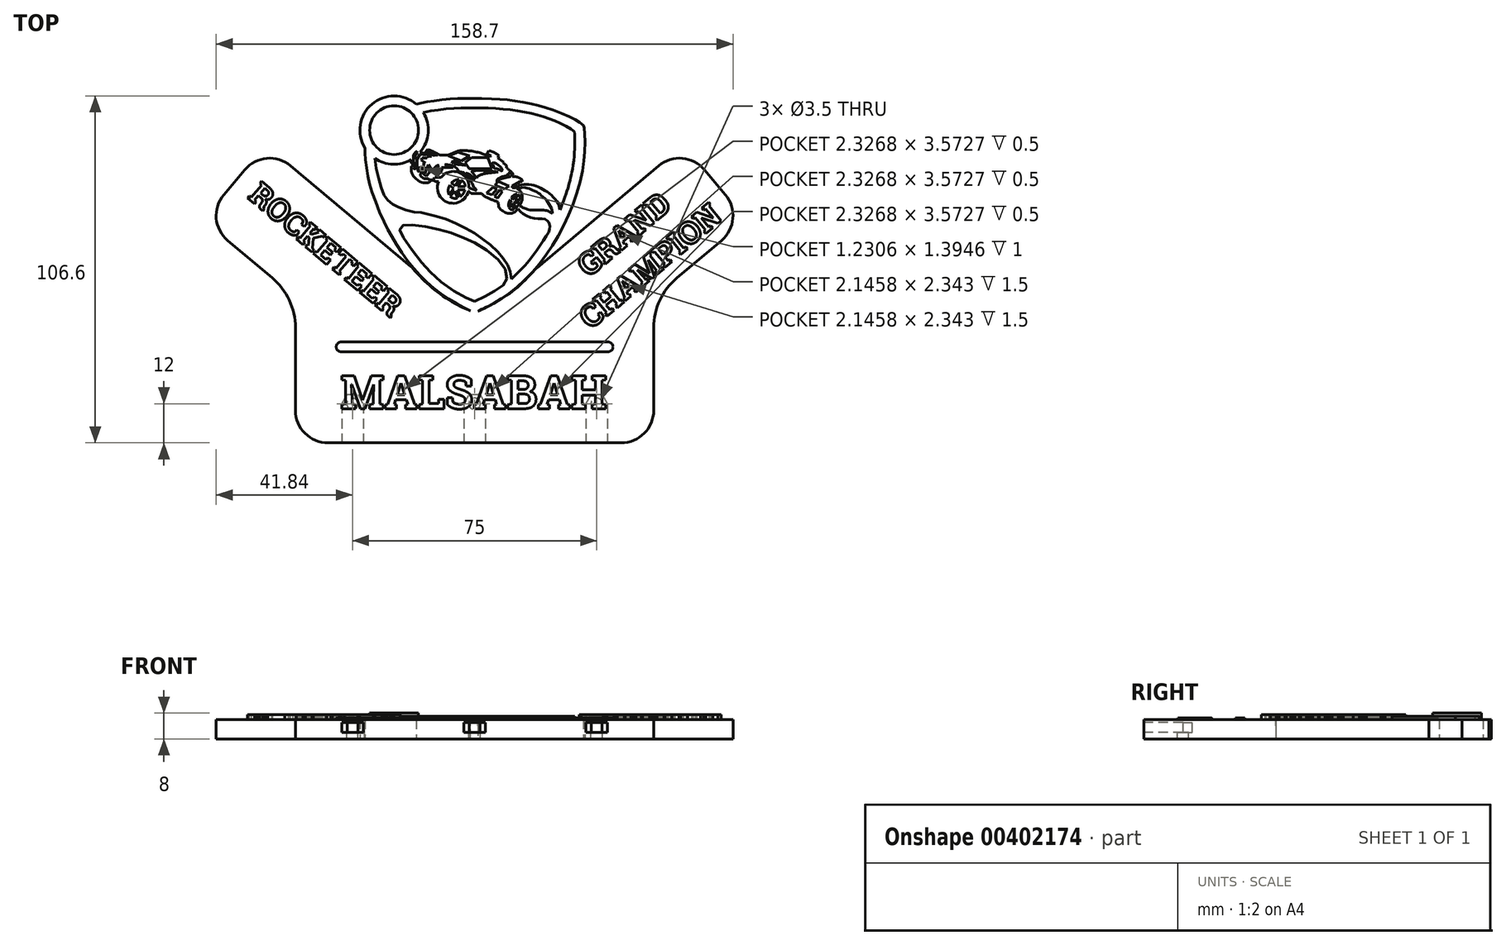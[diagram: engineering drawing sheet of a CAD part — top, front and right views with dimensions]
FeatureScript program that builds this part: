
annotation { "Feature Type Name" : "Feature", "Feature Type Description" : "" }
export const myFeature = defineFeature(function(context is Context, id is Id, definition is map)
    precondition{}
    {
        {
            var Q0;
            Q0=qCreatedBy(makeId("Top.planeOp"),FACE);
            var sketch = newSketch(context, id + "F0", { "sketchPlane" : qUnion([Q0])});
            skFitSpline(sketch, "E0", {"points": [v(34.26, 0.62) * mm, v(32.61, 1.76) * mm, v(29.36, 3.56) * mm, v(23.05, 5.92) * mm, v(18.77, 7.05) * mm, v(12.65, 8.2) * mm, v(7.75, 8.66) * mm, v(0, 8.9) * mm, v(-4.8, 8.82) * mm, v(-10.33, 8.27) * mm, v(-14.8, 7.6) * mm, v(-17.05, 7.08) * mm], "startDerivative": vector(-25.95, 18.48) * mm, "endDerivative": vector(-32.46, -8.72) * mm});
            skArc(sketch, "E1", {"start": v(-17.05, 7.08) * mm, "mid": v(-30.7, 7.12) * mm, "end": v(-32.86, -6.36) * mm});
            skFitSpline(sketch, "E2", {"points": [v(-32.86, -6.36) * mm, v(-32.85, -8.82) * mm, v(-32.03, -14.39) * mm, v(-30.66, -19.88) * mm, v(-27.23, -28.55) * mm, v(-24.25, -34.15) * mm, v(-19.95, -40.76) * mm, v(-14.92, -46.58) * mm, v(-9.53, -51.16) * mm, v(-3.63, -54.84) * mm, v(0.82, -56.98) * mm], "startDerivative": vector(-1.62, -34.7) * mm, "endDerivative": vector(48.34, -21.75) * mm});
            skFitSpline(sketch, "E3", {"points": [v(0.82, -56.98) * mm, v(4.3, -55.33) * mm, v(7.87, -53.37) * mm, v(11.6, -50.94) * mm, v(15.79, -47.36) * mm, v(20.03, -42.8) * mm, v(23.82, -37.65) * mm, v(27.13, -32.15) * mm, v(30.27, -25.64) * mm, v(32.62, -18.94) * mm, v(34.12, -12.35) * mm, v(34.59, -7.82) * mm, v(34.7, -3.26) * mm, v(34.59, -0.94) * mm, v(34.44, 0.44) * mm, v(34.4, 0.5) * mm, v(34.26, 0.62) * mm], "startDerivative": vector(56.12, 25.73) * mm, "endDerivative": vector(-12.98, 9.8) * mm});
            skSolve(sketch);
        }
        {
            var Q0;
            Q0 = qSketchRegion(id + "F0", true);
            extrude(context, id + "F1", {"entities" : qUnion([Q0]), "depth" : 2 * mm});
        }
        {
            var Q0;
            Q0=makeQuery(id+"F1.opExtrude","CAP_FACE",FACE,{"disambiguationData":[OSD([sQuery(id+"F0.wireOp",EDGE,"E0"),sQuery(id+"F0.wireOp",EDGE,"E1"),sQuery(id+"F0.wireOp",EDGE,"E2"),sQuery(id+"F0.wireOp",EDGE,"E3")])],"isStart":false});
            var sketch = newSketch(context, id + "F2", { "sketchPlane" : qUnion([Q0])});
            skCircle(sketch, "E4", {"center": v(-23.9, -0.88) * mm, "radius": 7.5 * mm});
            skArc(sketch, "E5", {"start": v(-29.8, -9.55) * mm, "mid": v(-24.25, -11.36) * mm, "end": v(-18.59, -9.92) * mm});
            skFitSpline(sketch, "E6", {"points": [v(-14.94, 4.56) * mm, v(-10.62, 5.31) * mm, v(-6, 5.79) * mm, v(-2.22, 5.95) * mm, v(1.06, 5.95) * mm, v(4.85, 5.91) * mm, v(8.93, 5.66) * mm, v(12.97, 5.22) * mm, v(16.92, 4.52) * mm, v(19.88, 3.8) * mm, v(22.63, 3) * mm, v(25.35, 2) * mm, v(27.78, 0.93) * mm, v(30.34, -0.54) * mm, v(31.49, -1.35) * mm], "startDerivative": vector(52.16, 10) * mm, "endDerivative": vector(21.73, -16.3) * mm});
            skFitSpline(sketch, "E7", {"points": [v(-29.8, -9.55) * mm, v(-29.43, -12.24) * mm, v(-28.74, -15.1) * mm, v(-28.13, -17.6) * mm, v(-27.56, -19.7) * mm, v(-26.75, -21.2) * mm, v(-26.19, -22.03) * mm, v(-25.6, -22.6) * mm, v(-24.77, -23.33) * mm, v(-23.73, -24.01) * mm, v(-22.77, -24.52) * mm, v(-21.14, -25.13) * mm, v(-19.24, -25.64) * mm, v(-17.51, -26.07) * mm, v(-16.1, -26.2) * mm, v(-15.02, -26.34) * mm, v(-13.75, -26.6) * mm, v(-12.07, -27.06) * mm, v(-9.37, -27.85) * mm, v(-6.76, -28.74) * mm, v(-3.83, -30.1) * mm, v(-1.06, -31.5) * mm, v(1.37, -32.98) * mm, v(3.42, -34.43) * mm, v(5.53, -36.06) * mm, v(7.67, -38.04) * mm, v(9.06, -39.62) * mm, v(10.31, -41.27) * mm, v(11.02, -42.56) * mm, v(11.6, -43.84) * mm, v(11.9, -45.02) * mm, v(12.07, -46.63) * mm], "startDerivative": vector(7.64, -69.25) * mm, "endDerivative": vector(4.25, -56.85) * mm});
            skFitSpline(sketch, "E8", {"points": [v(-17.23, -7.47) * mm, v(-17.72, -8.22) * mm, v(-17.96, -9.02) * mm, v(-18, -10.17) * mm, v(-18, -11.13) * mm, v(-17.98, -11.25) * mm, v(-17.72, -11.3) * mm, v(-17.7, -11.57) * mm, v(-17.96, -12.09) * mm, v(-17.9, -12.68) * mm, v(-17.23, -12.7) * mm, v(-17.08, -12.55) * mm, v(-17.2, -12.37) * mm, v(-17.23, -12.17) * mm, v(-17.08, -12.09) * mm, v(-17.08, -11.47) * mm, v(-17.25, -11.4) * mm, v(-17.25, -11.25) * mm, v(-17.03, -11.12) * mm, v(-17.02, -10.88) * mm, v(-17.01, -9.66) * mm, v(-17.68, -9.22) * mm, v(-17.68, -9.15) * mm, v(-16.8, -7.71) * mm], "startDerivative": vector(-8.9, -12.28) * mm, "endDerivative": vector(14.24, 22.86) * mm});
            skLineSegment(sketch, "E9", {"start": v(-18, -9.55) * mm, "end": v(-18, -8.73) * mm});
            skLineSegment(sketch, "E10", {"start": v(-18, -8.73) * mm, "end": v(-17.23, -7.47) * mm});
            skLineSegment(sketch, "E11", {"start": v(-17.23, -7.47) * mm, "end": v(-16.8, -7.4) * mm});
            skLineSegment(sketch, "E12", {"start": v(-16.8, -7.4) * mm, "end": v(-16.77, -7.63) * mm});
            skLineSegment(sketch, "E13", {"start": v(-16.77, -7.63) * mm, "end": v(-17.68, -9.22) * mm});
            skLineSegment(sketch, "E14", {"start": v(-17.68, -9.22) * mm, "end": v(-17.6, -9.26) * mm});
            skArc(sketch, "E15.trimOffspring", {"start": v(-15.88, -7.63) * mm, "mid": v(-13.45, -1.69) * mm, "end": v(-14.94, 4.56) * mm});
            skFitSpline(sketch, "E16", {"points": [v(-18.59, -9.92) * mm, v(-18.58, -10.96) * mm, v(-18.57, -11.08) * mm, v(-18.31, -11.1) * mm, v(-18.3, -11.85) * mm, v(-18.6, -11.92) * mm], "startDerivative": vector(0.17, -4.12) * mm, "endDerivative": vector(-2.08, 0.4) * mm});
            skFitSpline(sketch, "E17", {"points": [v(0.77, -53.51) * mm, v(3.27, -52.38) * mm, v(5.5, -51.11) * mm, v(7.6, -49.85) * mm, v(9.46, -48.65) * mm, v(10.34, -47.74) * mm, v(10.72, -46.7) * mm, v(10.75, -44.99) * mm, v(9.77, -42.84) * mm, v(7.85, -40.44) * mm, v(4.18, -37.57) * mm, v(0.8, -35.51) * mm, v(-1.4, -34.44) * mm, v(-4.75, -33.05) * mm, v(-8.7, -31.79) * mm, v(-11.32, -31.1) * mm, v(-15.43, -30.34) * mm, v(-18.87, -29.99) * mm, v(-20.76, -30.05) * mm, v(-21.42, -30.33) * mm, v(-21.8, -30.67) * mm, v(-22.06, -31.13) * mm, v(-21.98, -32.34) * mm, v(-21.12, -33.72) * mm, v(-18.6, -37.48) * mm, v(-15.51, -41.47) * mm, v(-13.22, -44.03) * mm, v(-10.28, -46.81) * mm, v(-6.36, -49.76) * mm, v(-2.82, -51.9) * mm, v(-0.24, -53.1) * mm, v(0.77, -53.51) * mm]});
            skFitSpline(sketch, "E18", {"points": [v(27.04, -25.26) * mm, v(27.54, -24.2) * mm, v(28.68, -21.14) * mm, v(29.32, -19.26) * mm, v(30.13, -16.28) * mm, v(30.54, -14.48) * mm, v(30.95, -12.73) * mm, v(31.4, -8.86) * mm, v(31.58, -6.01) * mm, v(31.58, -2.73) * mm, v(31.49, -1.35) * mm], "startDerivative": vector(6.36, 12.49) * mm, "endDerivative": vector(-1.45, 15.73) * mm});
            skFitSpline(sketch, "E19", {"points": [v(12.07, -46.63) * mm, v(14.9, -43.93) * mm, v(17.55, -41) * mm, v(19.56, -38.3) * mm, v(21.52, -35.51) * mm, v(23.04, -33.14) * mm, v(23.73, -31.9) * mm, v(23.9, -30.95) * mm, v(23.9, -29.9) * mm, v(23.6, -29.15) * mm, v(23, -28.57) * mm, v(22.36, -28.2) * mm, v(21.48, -28.14) * mm, v(20.17, -28.1) * mm, v(18.8, -27.92) * mm, v(17.3, -27.47) * mm, v(15.95, -26.77) * mm, v(14.95, -25.97) * mm, v(14.13, -25.03) * mm], "startDerivative": vector(33.43, 30.96) * mm, "endDerivative": vector(-16.34, 20.24) * mm});
            skFitSpline(sketch, "E20", {"points": [v(27.04, -25.26) * mm, v(26.7, -23.97) * mm, v(25.7, -22.25) * mm, v(24.03, -20.6) * mm, v(22.3, -19.32) * mm, v(20.39, -18.32) * mm, v(18.7, -17.75) * mm, v(16.52, -17.56) * mm, v(14.82, -17.75) * mm, v(13.4, -18.63) * mm], "startDerivative": vector(-2.7, 13.54) * mm, "endDerivative": vector(-13.15, -10.12) * mm});
            skFitSpline(sketch, "E21", {"points": [v(24.7, -26.5) * mm, v(24.6, -25.58) * mm, v(23.86, -23.9) * mm, v(22.5, -22.04) * mm, v(21.06, -20.73) * mm, v(19.9, -19.87) * mm, v(18.3, -19.13) * mm, v(17.04, -18.68) * mm, v(15.6, -18.5) * mm, v(13.93, -18.87) * mm], "startDerivative": vector(-0.28, 10.25) * mm, "endDerivative": vector(-14.78, -4.42) * mm});
            skFitSpline(sketch, "E22", {"points": [v(13.93, -18.87) * mm, v(14.45, -19.16) * mm, v(15.01, -19.78) * mm, v(15.38, -20.69) * mm, v(15.48, -21.73) * mm, v(15.27, -22.76) * mm, v(14.73, -24.1) * mm], "startDerivative": vector(3.99, -1.92) * mm, "endDerivative": vector(-3.03, -6.85) * mm});
            skFitSpline(sketch, "E23", {"points": [v(24.7, -26.5) * mm, v(24.15, -26.13) * mm, v(23.22, -25.68) * mm, v(21.78, -25.45) * mm, v(17.66, -25.39) * mm, v(16.56, -25.06) * mm, v(15.48, -24.56) * mm, v(14.73, -24.1) * mm], "startDerivative": vector(-5.09, 3.64) * mm, "endDerivative": vector(-6.08, 3.87) * mm});
            skLineSegment(sketch, "E24", {"start": v(-7.1, -8.78) * mm, "end": v(-4.3, -7.69) * mm});
            skLineSegment(sketch, "E25", {"start": v(-4.3, -7.69) * mm, "end": v(-0.72, -8.75) * mm});
            skLineSegment(sketch, "E26", {"start": v(-0.72, -8.75) * mm, "end": v(-3.26, -10.28) * mm});
            skLineSegment(sketch, "E27", {"start": v(-3.26, -10.28) * mm, "end": v(-7.1, -8.78) * mm});
            skEllipticalArc(sketch, "E28", {});
            skLineSegment(sketch, "E29", {"start": v(13.12, -22.2) * mm, "end": v(14.3, -20.69) * mm});
            skLineSegment(sketch, "E30", {"start": v(13.12, -22.2) * mm, "end": v(14.83, -22.2) * mm});
            skLineSegment(sketch, "E31", {"start": v(11.32, -24.4) * mm, "end": v(12.13, -23.16) * mm});
            skLineSegment(sketch, "E32", {"start": v(12.13, -23.16) * mm, "end": v(11.7, -22.24) * mm});
            skLineSegment(sketch, "E33", {"start": v(12.51, -22.2) * mm, "end": v(12.18, -21.5) * mm});
            skLineSegment(sketch, "E34", {"start": v(12.51, -22.2) * mm, "end": v(13.8, -20.54) * mm});
            skLineSegment(sketch, "E35", {"start": v(12.34, -23.47) * mm, "end": v(11.47, -24.8) * mm});
            skLineSegment(sketch, "E36", {"start": v(12.83, -23.18) * mm, "end": v(14.6, -23.18) * mm});
            skLineSegment(sketch, "E37", {"start": v(12.83, -23.18) * mm, "end": v(13.43, -24.85) * mm});
            skLineSegment(sketch, "E38", {"start": v(12.94, -25.16) * mm, "end": v(12.34, -23.47) * mm});
            skEllipticalArc(sketch, "E39.trimOffspring", {});
            skEllipticalArc(sketch, "E40.trimOffspring", {});
            skEllipticalArc(sketch, "E41.trimOffspring", {});
            skEllipticalArc(sketch, "E42.trimOffspring", {});
            skLineSegment(sketch, "E43", {"start": v(-2.12, -10.88) * mm, "end": v(0, -9.25) * mm});
            skLineSegment(sketch, "E44", {"start": v(0, -9.25) * mm, "end": v(4.93, -9.34) * mm});
            skLineSegment(sketch, "E45", {"start": v(4.93, -9.34) * mm, "end": v(6.11, -12.68) * mm});
            skLineSegment(sketch, "E46", {"start": v(6.11, -12.68) * mm, "end": v(-0.8, -12.7) * mm});
            skLineSegment(sketch, "E47", {"start": v(-0.8, -12.7) * mm, "end": v(-2.12, -10.88) * mm});
            skLineSegment(sketch, "E48", {"start": v(4.5, -20.17) * mm, "end": v(6.38, -18.4) * mm});
            skLineSegment(sketch, "E49", {"start": v(6.38, -18.4) * mm, "end": v(7.67, -19.02) * mm});
            skLineSegment(sketch, "E50", {"start": v(7.67, -19.02) * mm, "end": v(6.1, -20.7) * mm});
            skLineSegment(sketch, "E51", {"start": v(6.1, -20.7) * mm, "end": v(4.5, -20.17) * mm});
            skLineSegment(sketch, "E52", {"start": v(6.92, -21.24) * mm, "end": v(8.61, -19.24) * mm});
            skLineSegment(sketch, "E53", {"start": v(8.61, -19.24) * mm, "end": v(9.35, -19.66) * mm});
            skLineSegment(sketch, "E54", {"start": v(9.35, -19.66) * mm, "end": v(7.98, -21.76) * mm});
            skLineSegment(sketch, "E55", {"start": v(7.98, -21.76) * mm, "end": v(6.92, -21.24) * mm});
            skLineSegment(sketch, "E56", {"start": v(13.4, -18.63) * mm, "end": v(12.39, -18.63) * mm});
            skLineSegment(sketch, "E57", {"start": v(12.39, -18.63) * mm, "end": v(12.39, -18.09) * mm});
            skLineSegment(sketch, "E58", {"start": v(12.39, -18.09) * mm, "end": v(14.76, -16.68) * mm});
            skLineSegment(sketch, "E59", {"start": v(14.76, -16.68) * mm, "end": v(15.48, -16.68) * mm});
            skLineSegment(sketch, "E60", {"start": v(15.48, -16.68) * mm, "end": v(15.48, -16.22) * mm});
            skLineSegment(sketch, "E61", {"start": v(11.34, -18.1) * mm, "end": v(8.17, -16.72) * mm});
            skLineSegment(sketch, "E62", {"start": v(11.34, -18.1) * mm, "end": v(10.04, -18.97) * mm});
            skLineSegment(sketch, "E63", {"start": v(10.04, -18.97) * mm, "end": v(7.07, -17.8) * mm});
            skLineSegment(sketch, "E64", {"start": v(7.07, -17.8) * mm, "end": v(7.73, -17.16) * mm});
            skLineSegment(sketch, "E65", {"start": v(1.47, -19.45) * mm, "end": v(-0.91, -18.64) * mm});
            skLineSegment(sketch, "E66", {"start": v(-9.5, -15.36) * mm, "end": v(-11.32, -15.36) * mm});
            skLineSegment(sketch, "E67", {"start": v(-11.32, -15.36) * mm, "end": v(-11.32, -15.84) * mm});
            skLineSegment(sketch, "E68", {"start": v(-11.32, -15.84) * mm, "end": v(-12.06, -15.84) * mm});
            skLineSegment(sketch, "E69", {"start": v(-12.06, -15.84) * mm, "end": v(-12.06, -16.16) * mm});
            skLineSegment(sketch, "E70", {"start": v(-12.06, -16.16) * mm, "end": v(-13.1, -16.16) * mm});
            skLineSegment(sketch, "E71", {"start": v(-13.1, -16.16) * mm, "end": v(-13.45, -15.81) * mm});
            skLineSegment(sketch, "E72", {"start": v(-13.45, -15.81) * mm, "end": v(-14.82, -15.81) * mm});
            skLineSegment(sketch, "E73", {"start": v(-14.82, -15.81) * mm, "end": v(-15.83, -14.95) * mm});
            skLineSegment(sketch, "E74", {"start": v(-15.83, -14.95) * mm, "end": v(-15.7, -13.67) * mm});
            skLineSegment(sketch, "E75", {"start": v(-15.7, -13.67) * mm, "end": v(-14, -14.99) * mm});
            skLineSegment(sketch, "E76", {"start": v(-14, -14.99) * mm, "end": v(-12.83, -13.77) * mm});
            skLineSegment(sketch, "E77", {"start": v(-12.83, -13.77) * mm, "end": v(-13.75, -12.43) * mm});
            skLineSegment(sketch, "E78", {"start": v(-13.75, -12.43) * mm, "end": v(-13.44, -11.48) * mm});
            skLineSegment(sketch, "E79", {"start": v(-13.44, -11.48) * mm, "end": v(-12.23, -13.23) * mm});
            skLineSegment(sketch, "E80", {"start": v(-9.35, -12.33) * mm, "end": v(-5.78, -12.33) * mm});
            skLineSegment(sketch, "E81", {"start": v(-6.2, -11.04) * mm, "end": v(-5.76, -10.16) * mm});
            skLineSegment(sketch, "E82", {"start": v(-5.76, -10.16) * mm, "end": v(-1.96, -11.76) * mm});
            skLineSegment(sketch, "E83", {"start": v(-1.96, -11.76) * mm, "end": v(-5.57, -11.34) * mm});
            skLineSegment(sketch, "E84", {"start": v(-5.57, -11.34) * mm, "end": v(-5.26, -10.75) * mm});
            skLineSegment(sketch, "E85", {"start": v(-5.26, -10.75) * mm, "end": v(-5.57, -10.59) * mm});
            skLineSegment(sketch, "E86", {"start": v(-5.57, -10.59) * mm, "end": v(-5.89, -11.2) * mm});
            skLineSegment(sketch, "E87", {"start": v(-5.89, -11.2) * mm, "end": v(-6.2, -11.04) * mm});
            skLineSegment(sketch, "E88", {"start": v(-13.6, -7.36) * mm, "end": v(-13.84, -7.95) * mm});
            skLineSegment(sketch, "E89", {"start": v(-13.84, -7.95) * mm, "end": v(-11.6, -8.7) * mm});
            skLineSegment(sketch, "E90", {"start": v(-11.6, -8.7) * mm, "end": v(-10.52, -8.55) * mm});
            skLineSegment(sketch, "E91", {"start": v(-10.52, -8.55) * mm, "end": v(-13.6, -7.36) * mm});
            skLineSegment(sketch, "E92", {"start": v(-14.32, -10.92) * mm, "end": v(-15.6, -10.1) * mm});
            skLineSegment(sketch, "E93", {"start": v(-15.6, -10.1) * mm, "end": v(-15.3, -9.38) * mm});
            skLineSegment(sketch, "E94", {"start": v(-15.3, -9.38) * mm, "end": v(-13.84, -9.38) * mm});
            skLineSegment(sketch, "E95", {"start": v(-13.84, -9.38) * mm, "end": v(-13.84, -9.07) * mm});
            skLineSegment(sketch, "E96", {"start": v(-13.84, -9.07) * mm, "end": v(-12.35, -8.88) * mm});
            skLineSegment(sketch, "E97", {"start": v(-15.88, -7.63) * mm, "end": v(-14.63, -8.07) * mm});
            skLineSegment(sketch, "E98", {"start": v(-14.63, -8.07) * mm, "end": v(-13.53, -6.8) * mm});
            skLineSegment(sketch, "E99", {"start": v(-7.3, -8.55) * mm, "end": v(-4.25, -7.25) * mm});
            skLineSegment(sketch, "E100", {"start": v(5.53, -9.05) * mm, "end": v(5.94, -8.84) * mm});
            skLineSegment(sketch, "E101", {"start": v(5.94, -8.84) * mm, "end": v(4.64, -8.2) * mm});
            skLineSegment(sketch, "E102", {"start": v(4.64, -8.2) * mm, "end": v(5.13, -7.2) * mm});
            skEllipticalArc(sketch, "E103", {});
            skFitSpline(sketch, "E104", {"points": [v(14.13, -25.03) * mm, v(13.33, -25.9) * mm, v(12.37, -26.4) * mm, v(11.72, -26.51) * mm, v(10.7, -26.34) * mm, v(9.28, -25.58) * mm, v(8.35, -24.64) * mm, v(8.06, -22.98) * mm], "startDerivative": vector(-5.16, -6.57) * mm, "endDerivative": vector(-0.62, 10.73) * mm});
            skFitSpline(sketch, "E105", {"points": [v(8.06, -22.98) * mm, v(5.92, -22.16) * mm, v(4.08, -21.3) * mm, v(2.97, -20.4) * mm], "startDerivative": vector(-5.86, 2.23) * mm, "endDerivative": vector(-3.5, 3.24) * mm});
            skFitSpline(sketch, "E106", {"points": [v(2.97, -20.4) * mm, v(0, -20.4) * mm], "startDerivative": vector(-2.97, 0) * mm, "endDerivative": vector(-2.97, 0) * mm});
            skFitSpline(sketch, "E107", {"points": [v(0, -20.4) * mm, v(-0.53, -20.05) * mm, v(-1.12, -19.44) * mm], "startDerivative": vector(-1.16, 0.67) * mm, "endDerivative": vector(-1.09, 1.24) * mm});
            skEllipticalArc(sketch, "E108", {});
            skPoint(sketch, "E109.orphan", {"position": v(-0.93, -18.63) * mm});
            skFitSpline(sketch, "E110", {"points": [v(-10.27, -16.71) * mm, v(-11.15, -16.62) * mm, v(-11.97, -16.34) * mm, v(-12.4, -16.34) * mm, v(-13.34, -16.96) * mm, v(-14.4, -17.1) * mm, v(-15.69, -16.8) * mm, v(-17.44, -15.53) * mm, v(-18.28, -14.48) * mm, v(-18.62, -13.03) * mm, v(-18.6, -11.92) * mm], "startDerivative": vector(-9.86, 0.35) * mm, "endDerivative": vector(0.66, 10.71) * mm});
            skEllipticalArc(sketch, "E111.trimOffspring", {});
            skLineSegment(sketch, "E112", {"start": v(-10.58, -12.2) * mm, "end": v(-10.08, -11.7) * mm});
            skLineSegment(sketch, "E113", {"start": v(-10.08, -11.7) * mm, "end": v(-10.76, -11.7) * mm});
            skLineSegment(sketch, "E114", {"start": v(-10.76, -11.7) * mm, "end": v(-12.23, -13.23) * mm});
            skLineSegment(sketch, "E115", {"start": v(-16.55, -13.53) * mm, "end": v(-16.55, -12.11) * mm});
            skLineSegment(sketch, "E116", {"start": v(-16.55, -12.11) * mm, "end": v(-16.76, -12.11) * mm});
            skLineSegment(sketch, "E117", {"start": v(-16.76, -12.11) * mm, "end": v(-16.76, -9.8) * mm});
            skLineSegment(sketch, "E118", {"start": v(-16.76, -9.8) * mm, "end": v(-15.99, -8.3) * mm});
            skLineSegment(sketch, "E119", {"start": v(-15.99, -8.3) * mm, "end": v(-14.84, -8.3) * mm});
            skLineSegment(sketch, "E120", {"start": v(-12.35, -8.88) * mm, "end": v(-14.38, -8.2) * mm});
            skLineSegment(sketch, "E121", {"start": v(-14.38, -8.2) * mm, "end": v(-14.56, -8.78) * mm});
            skLineSegment(sketch, "E122", {"start": v(-14.56, -8.78) * mm, "end": v(-14.84, -8.3) * mm});
            skLineSegment(sketch, "E123", {"start": v(-16.55, -13.53) * mm, "end": v(-16.19, -13.73) * mm});
            skLineSegment(sketch, "E124", {"start": v(-16.19, -13.73) * mm, "end": v(-15.65, -13.15) * mm});
            skLineSegment(sketch, "E125", {"start": v(-15.65, -13.15) * mm, "end": v(-14.22, -14.2) * mm});
            skLineSegment(sketch, "E126", {"start": v(-14.22, -14.2) * mm, "end": v(-14.04, -12.7) * mm});
            skLineSegment(sketch, "E127", {"start": v(-14.04, -12.7) * mm, "end": v(-14.84, -12.3) * mm});
            skLineSegment(sketch, "E128", {"start": v(-14.84, -12.3) * mm, "end": v(-14.84, -10.92) * mm});
            skLineSegment(sketch, "E129", {"start": v(-14.84, -10.92) * mm, "end": v(-14.32, -10.92) * mm});
            skLineSegment(sketch, "E130", {"start": v(-15.75, -11.97) * mm, "end": v(-14.62, -12.8) * mm});
            skLineSegment(sketch, "E131", {"start": v(-14.62, -12.8) * mm, "end": v(-14.7, -13.37) * mm});
            skLineSegment(sketch, "E132", {"start": v(-14.7, -13.37) * mm, "end": v(-15.85, -12.52) * mm});
            skLineSegment(sketch, "E133", {"start": v(-15.85, -12.52) * mm, "end": v(-15.75, -11.97) * mm});
            skLineSegment(sketch, "E134", {"start": v(-7.3, -8.55) * mm, "end": v(-9.88, -8.55) * mm});
            skFitSpline(sketch, "E135", {"points": [v(-13.53, -6.8) * mm, v(-12.5, -7.2) * mm, v(-11.07, -7.86) * mm, v(-9.88, -8.55) * mm], "startDerivative": vector(3.23, -1.21) * mm, "endDerivative": vector(3.37, -2.05) * mm});
            skFitSpline(sketch, "E136", {"points": [v(-4.25, -7.25) * mm, v(-3, -7.17) * mm, v(-0.74, -7.25) * mm, v(1.82, -7.69) * mm, v(3.88, -8.36) * mm, v(5.53, -9.05) * mm], "startDerivative": vector(7.28, 0.65) * mm, "endDerivative": vector(8.45, -3.7) * mm});
            skFitSpline(sketch, "E137", {"points": [v(5.13, -7.2) * mm, v(6.32, -7.52) * mm, v(7.74, -8.3) * mm, v(8.38, -8.83) * mm], "startDerivative": vector(3.4, -0.62) * mm, "endDerivative": vector(1.99, -1.83) * mm});
            skFitSpline(sketch, "E138", {"points": [v(8.17, -16.72) * mm, v(8.17, -16.36) * mm, v(8.65, -16) * mm, v(9.83, -15.56) * mm, v(11.45, -15.22) * mm, v(12.02, -15.2) * mm], "startDerivative": vector(-0.58, 2.85) * mm, "endDerivative": vector(2.93, -0.12) * mm});
            skFitSpline(sketch, "E139", {"points": [v(12.4, -15.12) * mm, v(13.43, -15.2) * mm, v(14.69, -15.6) * mm, v(15.48, -16.22) * mm], "startDerivative": vector(3.06, -0.03) * mm, "endDerivative": vector(2.25, -2.08) * mm});
            skFitSpline(sketch, "E140", {"points": [v(7.73, -17.16) * mm, v(7.68, -16.31) * mm, v(7.8, -16.03) * mm, v(8.7, -15.46) * mm, v(11.07, -14.74) * mm], "startDerivative": vector(-0.48, 4.32) * mm, "endDerivative": vector(6.73, 1.7) * mm});
            skFitSpline(sketch, "E141", {"points": [v(12.68, -14.46) * mm, v(12.08, -13.7) * mm, v(11.34, -13.04) * mm, v(10.57, -12.33) * mm], "startDerivative": vector(-1.7, 2.41) * mm, "endDerivative": vector(-2.25, 2.12) * mm});
            skLineSegment(sketch, "E142", {"start": v(10.57, -12.33) * mm, "end": v(10.57, -11.66) * mm});
            skLineSegment(sketch, "E143", {"start": v(10.57, -11.66) * mm, "end": v(9.58, -10.96) * mm});
            skLineSegment(sketch, "E144", {"start": v(9.58, -10.96) * mm, "end": v(9.74, -10.73) * mm});
            skLineSegment(sketch, "E145", {"start": v(9.74, -10.73) * mm, "end": v(7.97, -9.47) * mm});
            skLineSegment(sketch, "E146", {"start": v(7.97, -9.47) * mm, "end": v(8.38, -8.83) * mm});
            skLineSegment(sketch, "E147", {"start": v(12.4, -15.12) * mm, "end": v(12.4, -14.86) * mm});
            skLineSegment(sketch, "E148", {"start": v(12.4, -14.86) * mm, "end": v(12.68, -14.46) * mm});
            skLineSegment(sketch, "E149", {"start": v(12.02, -15.2) * mm, "end": v(12.11, -14.85) * mm});
            skLineSegment(sketch, "E150", {"start": v(12.11, -14.85) * mm, "end": v(12.36, -14.5) * mm});
            skLineSegment(sketch, "E151", {"start": v(12.36, -14.5) * mm, "end": v(12, -14.18) * mm});
            skLineSegment(sketch, "E152", {"start": v(12, -14.18) * mm, "end": v(11.12, -14.18) * mm});
            skLineSegment(sketch, "E153", {"start": v(11.12, -14.18) * mm, "end": v(11.07, -14.74) * mm});
            skFitSpline(sketch, "E154", {"points": [v(0.9, -16.01) * mm, v(-0.12, -14.96) * mm, v(-1.05, -14.33) * mm, v(-1.82, -14.12) * mm], "startDerivative": vector(-2.63, 2.91) * mm, "endDerivative": vector(-2.72, 0.5) * mm});
            skFitSpline(sketch, "E155", {"points": [v(-1.82, -14.12) * mm, v(0, -16.08) * mm], "startDerivative": vector(1.82, -1.96) * mm, "endDerivative": vector(1.82, -1.96) * mm});
            skFitSpline(sketch, "E156", {"points": [v(0, -16.08) * mm, v(0.9, -16.01) * mm], "startDerivative": vector(0.9, 0.07) * mm, "endDerivative": vector(0.9, 0.07) * mm});
            skFitSpline(sketch, "E157", {"points": [v(-0.14, -13.35) * mm, v(3.8, -13.32) * mm, v(8.06, -13.76) * mm], "startDerivative": vector(7.98, 0.28) * mm, "endDerivative": vector(8.4, -1.1) * mm});
            skFitSpline(sketch, "E158", {"points": [v(1.47, -15.6) * mm, v(-0.14, -13.35) * mm], "startDerivative": vector(-1.6, 2.26) * mm, "endDerivative": vector(-1.6, 2.26) * mm});
            skFitSpline(sketch, "E159", {"points": [v(1.47, -15.6) * mm, v(1.71, -15.11) * mm, v(2.55, -14.66) * mm, v(3.78, -14.27) * mm, v(6.1, -13.93) * mm, v(8.06, -13.76) * mm], "startDerivative": vector(1.17, 4.08) * mm, "endDerivative": vector(7.7, 0.6) * mm});
            skFitSpline(sketch, "E160", {"points": [v(6.7, -10.8) * mm, v(6.35, -11) * mm, v(6.18, -11.29) * mm, v(6.35, -11.5) * mm, v(6.64, -11.85) * mm, v(6.9, -12.69) * mm, v(7.12, -12.69) * mm, v(7.93, -12.77) * mm, v(8.91, -13.35) * mm, v(9.24, -13.35) * mm, v(9.2, -12.86) * mm, v(8.35, -11.81) * mm, v(7.63, -11.27) * mm, v(6.7, -10.8) * mm]});
            skFitSpline(sketch, "E161", {"points": [v(1.47, -19.45) * mm, v(1.08, -18.87) * mm, v(0.66, -18.49) * mm, v(0.17, -17.4) * mm, v(-1.03, -15.69) * mm, v(-1.81, -14.73) * mm, v(-2.6, -13.96) * mm, v(-3.72, -13.63) * mm, v(-4.07, -13.43) * mm, v(-4.4, -12.94) * mm, v(-4.9, -12.42) * mm, v(-5.12, -12.14) * mm, v(-6.65, -11.61) * mm, v(-7.88, -11.43) * mm, v(-8.3, -11.43) * mm], "startDerivative": vector(-5.73, 10.19) * mm, "endDerivative": vector(-7.72, -0.28) * mm});
            skFitSpline(sketch, "E162", {"points": [v(-5.78, -12.33) * mm, v(-6.35, -11.94) * mm, v(-7.54, -11.68) * mm, v(-8.3, -11.43) * mm], "startDerivative": vector(-1.66, 1.46) * mm, "endDerivative": vector(-2.2, 0.86) * mm});
            skEllipticalArc(sketch, "E163", {});
            skLineSegment(sketch, "E164", {"start": v(-4.36, -18.24) * mm, "end": v(-3.2, -16.29) * mm});
            skLineSegment(sketch, "E165", {"start": v(-4.36, -18.24) * mm, "end": v(-2.04, -18.24) * mm});
            skLineSegment(sketch, "E166", {"start": v(-4.44, -19.21) * mm, "end": v(-2.13, -19.21) * mm});
            skLineSegment(sketch, "E167", {"start": v(-4.44, -19.21) * mm, "end": v(-3.56, -21.31) * mm});
            skLineSegment(sketch, "E168", {"start": v(-5.24, -19.62) * mm, "end": v(-4.34, -21.72) * mm});
            skLineSegment(sketch, "E169", {"start": v(-5.24, -19.62) * mm, "end": v(-6.64, -21.25) * mm});
            skLineSegment(sketch, "E170", {"start": v(-7.03, -20.7) * mm, "end": v(-5.68, -18.8) * mm});
            skLineSegment(sketch, "E171", {"start": v(-5.68, -18.8) * mm, "end": v(-6.84, -17.84) * mm});
            skLineSegment(sketch, "E172", {"start": v(-5.1, -18.03) * mm, "end": v(-3.94, -16.08) * mm});
            skLineSegment(sketch, "E173", {"start": v(-5.1, -18.03) * mm, "end": v(-6.3, -17.08) * mm});
            skEllipticalArc(sketch, "E174.trimOffspring", {});
            skEllipticalArc(sketch, "E175.trimOffspring", {});
            skEllipticalArc(sketch, "E176.trimOffspring", {});
            skEllipticalArc(sketch, "E177.trimOffspring", {});
            const initialGuessF2  = {"E28": [0.013050052337348461, -0.02292713336646557, 0.4552293076518856, 0.8903742344962511, 0.002567609329112346, 0.0015176400421892321, 5.313404945174112, 6.22491118650798], "E39.trimOffspring": [0.013050052337348461, -0.02292713336646557, 0.4552293076518856, 0.8903742344962511, 0.002567609329112346, 0.0015176400421892321, 4.071520655521499, 4.901137376991816], "E40.trimOffspring": [0.013050052337348461, -0.02292713336646557, 0.4552293076518856, 0.8903742344962511, 0.002567609329112346, 0.0015176400421892321, 2.7691985795929615, 3.7956728786048983], "E41.trimOffspring": [0.013050052337348461, -0.02292713336646557, 0.4552293076518856, 0.8903742344962511, 0.002567609329112346, 0.0015176400421892321, 1.5707963267948961, 2.5331685271344946], "E42.trimOffspring": [0.013050052337348461, -0.02292713336646557, 0.4552293076518856, 0.8903742344962511, 0.002567609329112346, 0.0015176400421892321, 0.2801564065357715, 1.2215433865438743], "E103": [-0.010266351513564587, -0.013160503469407558, 0.7384191084470064, 0.67434206474187, 0.0012362104379512009, 0.0009804556465305818, 1.2251866819937565, 0], "E108": [-0.005758708342909813, -0.018453748896718025, 0.4243013860770925, 0.9055210288961036, 0.0049140878670050825, 0.004840537962114324, 5.107671988170148, 1.3208876384781154], "E111.trimOffspring": [-0.005758708342909813, -0.018453748896718025, 0.4243013860770925, 0.9055210288961036, 0.0049140878670050825, 0.004840537962114324, 1.6395337719154794, 4.9213604411289955], "E163": [-0.004662276711314917, -0.01896517351269722, 0.5254930823535597, 0.8507978728220674, 0.0030484361421130135, 0.0024509906275484205, 0.3759147567652964, 1.3244632397862512], "E174.trimOffspring": [-0.004662276711314917, -0.01896517351269722, 0.5254930823535597, 0.8507978728220674, 0.0030484361421130135, 0.0024509906275484205, 1.632610495109953, 2.6717597258003964], "E175.trimOffspring": [-0.004662276711314917, -0.01896517351269722, 0.5254930823535597, 0.8507978728220674, 0.0030484361421130135, 0.0024509906275484205, 2.9431830061992965, 3.920722245962533], "E176.trimOffspring": [-0.004662276711314917, -0.01896517351269722, 0.5254930823535597, 0.8507978728220674, 0.0030484361421130135, 0.0024509906275484205, 4.227758848077727, 5.087713024134253], "E177.trimOffspring": [-0.004662276711314917, -0.01896517351269722, 0.5254930823535597, 0.8507978728220674, 0.0030484361421130135, 0.0024509906275484205, 5.425088584935971, 0.06817217455088062]};
            skSetInitialGuess(sketch, initialGuessF2);
            skSolve(sketch);
        }
        {
            var Q0;
            Q0 = qSketchRegion(id + "F2", true);
            extrude(context, id + "F3", {"entities" : qUnion([Q0]), "operationType" : NewBodyOperationType.ADD, "depth" : 0.5 * mm});
        }
        {
            var Q0;
            Q0=makeQuery(id+"F3.opExtrude","CAP_FACE",FACE,{"disambiguationData":[OSD([sQuery(id+"F2.wireOp",EDGE,"E4")])],"isStart":false});
            extrude(context, id + "F4", {"entities" : qUnion([Q0]), "operationType" : NewBodyOperationType.ADD, "depth" : 0.5 * mm});
        }
        {
            var Q0;
            {var subQ0=sQuery(id+"F0.wireOp",EDGE,"E1");var subQ1=sQuery(id+"F0.wireOp",EDGE,"E3");var subQ2=sQuery(id+"F0.wireOp",EDGE,"E0");var subQ3=sQuery(id+"F0.wireOp",EDGE,"E2");Q0=makeQuery(id+"F3.boolean.opBoolean","SPLIT",FACE,{"disambiguationData":[TD([makeQuery(id+"F1.opExtrude","SWEPT_FACE",FACE,{"disambiguationData":[OSD([subQ2])]})])],"derivedFrom":makeQuery(id+"F1.opExtrude","CAP_FACE",FACE,{"disambiguationData":[OSD([subQ2,subQ0,subQ3,subQ1])],"isStart":false})});}
            var sketch = newSketch(context, id + "F5", { "sketchPlane" : qUnion([Q0])});
            skFitSpline(sketch, "E178.0", {"points": [v(0.82, -56.98) * mm, v(1.98, -56.45) * mm, v(4.34, -55.37) * mm, v(7.93, -53.38) * mm, v(11.72, -51) * mm, v(15.91, -47.4) * mm, v(20.14, -42.87) * mm, v(23.9, -37.68) * mm, v(27.23, -32.19) * mm, v(30.4, -25.64) * mm, v(32.72, -19.11) * mm, v(34.23, -12.38) * mm, v(34.62, -8.01) * mm, v(34.76, -3.28) * mm, v(34.61, -1.19) * mm, v(34.46, 0.43) * mm, v(34.42, 0.5) * mm, v(34.32, 0.58) * mm, v(34.26, 0.62) * mm]});
            skFitSpline(sketch, "E179.0", {"points": [v(-32.86, -6.36) * mm, v(-32.9, -7.09) * mm, v(-32.96, -8.9) * mm, v(-32.03, -14.7) * mm, v(-30.87, -19.84) * mm, v(-27.3, -28.77) * mm, v(-24.36, -34.08) * mm, v(-20.09, -40.94) * mm, v(-15.06, -46.69) * mm, v(-9.72, -51.25) * mm, v(-3.75, -54.93) * mm, v(-0.61, -56.34) * mm, v(0.82, -56.98) * mm]});
            skLineSegment(sketch, "E180", {"start": v(19.02, -43.98) * mm, "end": v(64.98, -5.41) * mm});
            skLineSegment(sketch, "E181", {"start": v(64.98, -5.41) * mm, "end": v(84.27, -28.4) * mm});
            skLineSegment(sketch, "E182", {"start": v(84.27, -28.4) * mm, "end": v(55.82, -52.26) * mm});
            skLineSegment(sketch, "E183", {"start": v(55.82, -52.26) * mm, "end": v(55.82, -96.98) * mm});
            skLineSegment(sketch, "E184", {"start": v(55.82, -96.98) * mm, "end": v(0.82, -96.98) * mm});
            skLineSegment(sketch, "E185", {"start": v(0.82, -56.98) * mm, "end": v(0.82, -94.5) * mm, "construction": true});
            skLineSegment(sketch, "E186", {"start": v(0.82, -96.98) * mm, "end": v(-54.18, -96.98) * mm});
            skLineSegment(sketch, "E187", {"start": v(-54.18, -96.98) * mm, "end": v(-54.18, -52.25) * mm});
            skLineSegment(sketch, "E188", {"start": v(-54.18, -52.25) * mm, "end": v(-82.61, -28.4) * mm});
            skLineSegment(sketch, "E189", {"start": v(-82.61, -28.4) * mm, "end": v(-63.33, -5.41) * mm});
            skLineSegment(sketch, "E190", {"start": v(-63.33, -5.41) * mm, "end": v(-17.37, -43.98) * mm});
            skLineSegment(sketch, "E191", {"start": v(19.02, -43.98) * mm, "end": v(-17.37, -43.98) * mm, "construction": true});
            skPoint(sketch, "E192.orphan", {"position": v(34.26, 0.62) * mm});
            skPoint(sketch, "E193.orphan", {"position": v(-32.86, -6.36) * mm});
            skSolve(sketch);
        }
        {
            var Q0;
            Q0 = qSketchRegion(id + "F5", true);
            var Q1;
            Q1=makeQuery(id+"F1.opExtrude","CAP_FACE",FACE,{"disambiguationData":[OSD([sQuery(id+"F0.wireOp",EDGE,"E0"),sQuery(id+"F0.wireOp",EDGE,"E1"),sQuery(id+"F0.wireOp",EDGE,"E2"),sQuery(id+"F0.wireOp",EDGE,"E3")])],"isStart":true});
            extrude(context, id + "F6", {"entities" : qUnion([Q0]), "operationType" : NewBodyOperationType.ADD, "endBound" : BoundingType.UP_TO_SURFACE, "oppositeDirection" : true, "endBoundEntityFace" : qUnion([Q1]), "depth" : 25 * mm});
        }
        {
            var Q0;
            Q0=makeQuery(id+"F6.opExtrude","SWEPT_EDGE",EDGE,{"disambiguationData":[OSD([sQuery(id+"F0.wireOp",EDGE,"E3"),sQuery(id+"F5.wireOp",EDGE,"E178.0"),sQuery(id+"F5.wireOp",EDGE,"E180")])]});
            var Q1;
            Q1=makeQuery(id+"F6.opExtrude","SWEPT_EDGE",EDGE,{"disambiguationData":[OSD([sQuery(id+"F0.wireOp",EDGE,"E2"),sQuery(id+"F5.wireOp",EDGE,"E179.0"),sQuery(id+"F5.wireOp",EDGE,"E190")])]});
            fillet(context, id + "F7", {"entities" : qUnion([Q0, Q1]), "radius" : 5 * mm, "tangentPropagation" : true, "allowEdgeOverflow" : false});
        }
        {
            var Q0;
            {var subQ0=sQuery(id+"F0.wireOp",EDGE,"E1");var subQ1=sQuery(id+"F0.wireOp",EDGE,"E3");var subQ2=sQuery(id+"F0.wireOp",EDGE,"E0");var subQ3=sQuery(id+"F0.wireOp",EDGE,"E2");Q0=makeQuery(id+"F6.boolean.opBoolean","MERGE",FACE,{"derivedFrom":[makeQuery(id+"F3.boolean.opBoolean","SPLIT",FACE,{"disambiguationData":[TD([makeQuery(id+"F1.opExtrude","SWEPT_FACE",FACE,{"disambiguationData":[OSD([subQ2])]})])],"derivedFrom":makeQuery(id+"F1.opExtrude","CAP_FACE",FACE,{"disambiguationData":[OSD([subQ2,subQ0,subQ3,subQ1])],"isStart":false})}),makeQuery(id+"F6.opExtrude","CAP_FACE",FACE,{"disambiguationData":[OSD([sQuery(id+"F5.wireOp",EDGE,"E178.0"),sQuery(id+"F5.wireOp",EDGE,"E179.0"),sQuery(id+"F5.wireOp",EDGE,"E180"),sQuery(id+"F5.wireOp",EDGE,"E181"),sQuery(id+"F5.wireOp",EDGE,"E182"),sQuery(id+"F5.wireOp",EDGE,"E183"),sQuery(id+"F5.wireOp",EDGE,"E184"),sQuery(id+"F5.wireOp",EDGE,"E186"),sQuery(id+"F5.wireOp",EDGE,"E187"),sQuery(id+"F5.wireOp",EDGE,"E188"),sQuery(id+"F5.wireOp",EDGE,"E189"),sQuery(id+"F5.wireOp",EDGE,"E190")])],"isStart":true})]});}
            var sketch = newSketch(context, id + "F8", { "sketchPlane" : qUnion([Q0])});
            skText(sketch, "E194", { "text": "ROCKETEER", "fontName": "RobotoSlab-Bold.ttf"});
            skText(sketch, "E195", { "text": "GRAND", "fontName": "RobotoSlab-Bold.ttf"});
            skText(sketch, "E196", { "text": "CHAMPION", "fontName": "RobotoSlab-Bold.ttf"});
            skLineSegment(sketch, "E197", {"start": v(60.06, -48.7) * mm, "end": v(38.18, -22.64) * mm, "construction": true});
            skLineSegment(sketch, "E198", {"start": v(-55.8, -50.9) * mm, "end": v(-32.4, -23) * mm, "construction": true});
            const initialGuessF8  = {"E194": [-0.0691, -0.02161, 0.76604, -0.64279, 0.00688], "E195": [0.0359, -0.04626, 0.76604, 0.64279, 0.00688], "E196": [0.03649, -0.06228, 0.76604, 0.64279, 0.00688]};
            skSetInitialGuess(sketch, initialGuessF8);
            skSolve(sketch);
        }
        {
            var Q0;
            Q0 = qSketchRegion(id + "F8", true);
            extrude(context, id + "F9", {"entities" : qUnion([Q0]), "operationType" : NewBodyOperationType.ADD, "depth" : 0.5 * mm});
        }
        {
            var Q0;
            Q0=makeQuery(id+"F6.opExtrude","SWEPT_EDGE",EDGE,{"disambiguationData":[OSD([sQuery(id+"F5.wireOp",EDGE,"E180"),sQuery(id+"F5.wireOp",EDGE,"E181")])]});
            var Q1;
            Q1=makeQuery(id+"F6.opExtrude","SWEPT_EDGE",EDGE,{"disambiguationData":[OSD([sQuery(id+"F5.wireOp",EDGE,"E181"),sQuery(id+"F5.wireOp",EDGE,"E182")])]});
            var Q2;
            Q2=makeQuery(id+"F6.opExtrude","SWEPT_EDGE",EDGE,{"disambiguationData":[OSD([sQuery(id+"F5.wireOp",EDGE,"E189"),sQuery(id+"F5.wireOp",EDGE,"E190")])]});
            var Q3;
            Q3=makeQuery(id+"F6.opExtrude","SWEPT_EDGE",EDGE,{"disambiguationData":[OSD([sQuery(id+"F5.wireOp",EDGE,"E188"),sQuery(id+"F5.wireOp",EDGE,"E189")])]});
            fillet(context, id + "F10", {"entities" : qUnion([Q0, Q1, Q2, Q3]), "radius" : 10 * mm, "tangentPropagation" : true, "allowEdgeOverflow" : false});
        }
        {
            var Q0;
            Q0=makeQuery(id+"F6.opExtrude","SWEPT_EDGE",EDGE,{"disambiguationData":[OSD([sQuery(id+"F5.wireOp",EDGE,"E182"),sQuery(id+"F5.wireOp",EDGE,"E183")])]});
            var Q1;
            Q1=makeQuery(id+"F6.opExtrude","SWEPT_EDGE",EDGE,{"disambiguationData":[OSD([sQuery(id+"F5.wireOp",EDGE,"E187"),sQuery(id+"F5.wireOp",EDGE,"E188")])]});
            fillet(context, id + "F11", {"entities" : qUnion([Q0, Q1]), "radius" : 20 * mm, "tangentPropagation" : true, "allowEdgeOverflow" : false});
        }
        {
            var Q0;
            {var subQ56=sQuery(id+"F5.wireOp",EDGE,"E190");var subQ57=sQuery(id+"F5.wireOp",EDGE,"E179.0");var subQ58=sQuery(id+"F0.wireOp",EDGE,"E2");var subQ85=sQuery(id+"F5.wireOp",EDGE,"E183");var subQ98=sQuery(id+"F0.wireOp",EDGE,"E1");var subQ102=sQuery(id+"F5.wireOp",EDGE,"E188");var subQ103=sQuery(id+"F5.wireOp",EDGE,"E182");var subQ106=sQuery(id+"F0.wireOp",EDGE,"E3");var subQ112=sQuery(id+"F0.wireOp",EDGE,"E0");var subQ113=makeQuery(id+"F1.opExtrude","SWEPT_FACE",FACE,{"disambiguationData":[OSD([subQ112])]});var subQ115=sQuery(id+"F5.wireOp",EDGE,"E187");var subQ120=sQuery(id+"F5.wireOp",EDGE,"E189");var subQ122=sQuery(id+"F5.wireOp",EDGE,"E186");var subQ123=sQuery(id+"F5.wireOp",EDGE,"E184");var subQ133=sQuery(id+"F5.wireOp",EDGE,"E180");var subQ135=sQuery(id+"F5.wireOp",EDGE,"E181");var subQ189=sQuery(id+"F5.wireOp",EDGE,"E178.0");Q0=makeQuery(id+"F9.boolean.opBoolean","SPLIT",FACE,{"disambiguationData":[TD([subQ113])],"derivedFrom":makeQuery(id+"F6.boolean.opBoolean","MERGE",FACE,{"derivedFrom":[makeQuery(id+"F3.boolean.opBoolean","SPLIT",FACE,{"disambiguationData":[TD([subQ113])],"derivedFrom":makeQuery(id+"F1.opExtrude","CAP_FACE",FACE,{"disambiguationData":[OSD([subQ112,subQ98,subQ58,subQ106])],"isStart":false})}),makeQuery(id+"F6.opExtrude","CAP_FACE",FACE,{"disambiguationData":[OSD([subQ189,subQ57,subQ133,subQ135,subQ103,subQ85,subQ123,subQ122,subQ115,subQ102,subQ120,subQ56])],"isStart":true})]})});}
            var sketch = newSketch(context, id + "F12", { "sketchPlane" : qUnion([Q0])});
            skText(sketch, "E199", { "text": "MALSABAH", "fontName": "RobotoSlab-Bold.ttf"});
            skLineSegment(sketch, "E200", {"start": v(0.82, -96.98) * mm, "end": v(0.82, -63.22) * mm, "construction": true});
            const initialGuessF12  = {"E199": [-0.0403, -0.08649, 1, 0, 0.01027]};
            skSetInitialGuess(sketch, initialGuessF12);
            skSolve(sketch);
        }
        {
            var Q0;
            Q0 = qSketchRegion(id + "F12", true);
            extrude(context, id + "F13", {"entities" : qUnion([Q0]), "operationType" : NewBodyOperationType.ADD, "depth" : 0.5 * mm});
        }
        {
            var Q0;
            Q0=makeQuery(id+"F6.opExtrude","SWEPT_EDGE",EDGE,{"disambiguationData":[OSD([sQuery(id+"F5.wireOp",EDGE,"E183"),sQuery(id+"F5.wireOp",EDGE,"E184")])]});
            var Q1;
            Q1=makeQuery(id+"F6.opExtrude","SWEPT_EDGE",EDGE,{"disambiguationData":[OSD([sQuery(id+"F5.wireOp",EDGE,"E186"),sQuery(id+"F5.wireOp",EDGE,"E187")])]});
            fillet(context, id + "F14", {"entities" : qUnion([Q0, Q1]), "radius" : 10 * mm, "tangentPropagation" : true, "allowEdgeOverflow" : false});
        }
        {
            var Q0;
            {var subQ189=sQuery(id+"F5.wireOp",EDGE,"E190");var subQ190=sQuery(id+"F5.wireOp",EDGE,"E179.0");var subQ191=sQuery(id+"F0.wireOp",EDGE,"E2");var subQ256=sQuery(id+"F5.wireOp",EDGE,"E183");var subQ284=sQuery(id+"F0.wireOp",EDGE,"E1");var subQ290=sQuery(id+"F5.wireOp",EDGE,"E188");var subQ297=sQuery(id+"F5.wireOp",EDGE,"E182");var subQ303=sQuery(id+"F0.wireOp",EDGE,"E3");var subQ316=sQuery(id+"F0.wireOp",EDGE,"E0");var subQ317=makeQuery(id+"F1.opExtrude","SWEPT_FACE",FACE,{"disambiguationData":[OSD([subQ316])]});var subQ322=sQuery(id+"F5.wireOp",EDGE,"E187");var subQ334=sQuery(id+"F5.wireOp",EDGE,"E189");var subQ342=sQuery(id+"F5.wireOp",EDGE,"E186");var subQ343=sQuery(id+"F5.wireOp",EDGE,"E184");var subQ363=sQuery(id+"F5.wireOp",EDGE,"E180");var subQ367=sQuery(id+"F5.wireOp",EDGE,"E181");var subQ467=sQuery(id+"F5.wireOp",EDGE,"E178.0");Q0=makeQuery(id+"F13.boolean.opBoolean","SPLIT",FACE,{"disambiguationData":[TD([subQ317])],"derivedFrom":makeQuery(id+"F9.boolean.opBoolean","SPLIT",FACE,{"disambiguationData":[TD([subQ317])],"derivedFrom":makeQuery(id+"F6.boolean.opBoolean","MERGE",FACE,{"derivedFrom":[makeQuery(id+"F3.boolean.opBoolean","SPLIT",FACE,{"disambiguationData":[TD([subQ317])],"derivedFrom":makeQuery(id+"F1.opExtrude","CAP_FACE",FACE,{"disambiguationData":[OSD([subQ316,subQ284,subQ191,subQ303])],"isStart":false})}),makeQuery(id+"F6.opExtrude","CAP_FACE",FACE,{"disambiguationData":[OSD([subQ467,subQ190,subQ363,subQ367,subQ297,subQ256,subQ343,subQ342,subQ322,subQ290,subQ334,subQ189])],"isStart":true})]})})});}
            var sketch = newSketch(context, id + "F15", { "sketchPlane" : qUnion([Q0])});
            skLineSegment(sketch, "E201", {"start": v(-41.68, -68.98) * mm, "end": v(43.32, -68.98) * mm});
            skLineSegment(sketch, "E202", {"start": v(0.82, -96.98) * mm, "end": v(0.82, -68.98) * mm, "construction": true});
            skLineSegment(sketch, "E203", {"start": v(43.32, -68.98) * mm, "end": v(43.32, -65.98) * mm});
            skLineSegment(sketch, "E204", {"start": v(43.32, -65.98) * mm, "end": v(-41.68, -65.98) * mm});
            skLineSegment(sketch, "E205", {"start": v(-41.68, -65.98) * mm, "end": v(-41.68, -68.98) * mm});
            skSolve(sketch);
        }
        {
            var Q0;
            Q0 = qSketchRegion(id + "F15", true);
            extrude(context, id + "F16", {"entities" : qUnion([Q0]), "operationType" : NewBodyOperationType.ADD, "depth" : 0.5 * mm});
        }
        {
            var Q0;
            Q0=makeQuery(id+"F16.opExtrude","SWEPT_EDGE",EDGE,{"disambiguationData":[OSD([sQuery(id+"F15.wireOp",EDGE,"E204"),sQuery(id+"F15.wireOp",EDGE,"E205")])]});
            var Q1;
            Q1=makeQuery(id+"F16.opExtrude","SWEPT_EDGE",EDGE,{"disambiguationData":[OSD([sQuery(id+"F15.wireOp",EDGE,"E201"),sQuery(id+"F15.wireOp",EDGE,"E205")])]});
            var Q2;
            Q2=makeQuery(id+"F16.opExtrude","SWEPT_EDGE",EDGE,{"disambiguationData":[OSD([sQuery(id+"F15.wireOp",EDGE,"E201"),sQuery(id+"F15.wireOp",EDGE,"E203")])]});
            var Q3;
            Q3=makeQuery(id+"F16.opExtrude","SWEPT_EDGE",EDGE,{"disambiguationData":[OSD([sQuery(id+"F15.wireOp",EDGE,"E203"),sQuery(id+"F15.wireOp",EDGE,"E204")])]});
            fillet(context, id + "F17", {"entities" : qUnion([Q0, Q1, Q2, Q3]), "radius" : 1.5 * mm, "tangentPropagation" : true, "allowEdgeOverflow" : false});
        }
        {
            var Q0;
            Q0=makeQuery(id+"F3.opExtrude","CAP_FACE",FACE,{"disambiguationData":[OSD([sQuery(id+"F2.wireOp",EDGE,"E5"),sQuery(id+"F2.wireOp",EDGE,"E7"),sQuery(id+"F2.wireOp",EDGE,"E16"),sQuery(id+"F2.wireOp",EDGE,"E19"),sQuery(id+"F2.wireOp",EDGE,"E104"),sQuery(id+"F2.wireOp",EDGE,"E105"),sQuery(id+"F2.wireOp",EDGE,"E106"),sQuery(id+"F2.wireOp",EDGE,"E107"),sQuery(id+"F2.wireOp",EDGE,"E110"),sQuery(id+"F2.wireOp",EDGE,"E111.trimOffspring")])],"isStart":false});
            var Q1;
            Q1=makeQuery(id+"F3.opExtrude","CAP_FACE",FACE,{"disambiguationData":[OSD([sQuery(id+"F2.wireOp",EDGE,"E17")])],"isStart":false});
            var Q2;
            Q2=makeQuery(id+"F3.opExtrude","CAP_FACE",FACE,{"disambiguationData":[OSD([sQuery(id+"F2.wireOp",EDGE,"E21"),sQuery(id+"F2.wireOp",EDGE,"E22"),sQuery(id+"F2.wireOp",EDGE,"E23")])],"isStart":false});
            var Q3;
            Q3=makeQuery(id+"F3.opExtrude","CAP_FACE",FACE,{"disambiguationData":[OSD([sQuery(id+"F2.wireOp",EDGE,"E35"),sQuery(id+"F2.wireOp",EDGE,"E38"),sQuery(id+"F2.wireOp",EDGE,"E40.trimOffspring")])],"isStart":false});
            var Q4;
            Q4=makeQuery(id+"F3.opExtrude","CAP_FACE",FACE,{"disambiguationData":[OSD([sQuery(id+"F2.wireOp",EDGE,"E36"),sQuery(id+"F2.wireOp",EDGE,"E37"),sQuery(id+"F2.wireOp",EDGE,"E39.trimOffspring")])],"isStart":false});
            var Q5;
            Q5=makeQuery(id+"F3.opExtrude","CAP_FACE",FACE,{"disambiguationData":[OSD([sQuery(id+"F2.wireOp",EDGE,"E6"),sQuery(id+"F2.wireOp",EDGE,"E15.trimOffspring"),sQuery(id+"F2.wireOp",EDGE,"E18"),sQuery(id+"F2.wireOp",EDGE,"E20"),sQuery(id+"F2.wireOp",EDGE,"E56"),sQuery(id+"F2.wireOp",EDGE,"E57"),sQuery(id+"F2.wireOp",EDGE,"E58"),sQuery(id+"F2.wireOp",EDGE,"E59"),sQuery(id+"F2.wireOp",EDGE,"E60"),sQuery(id+"F2.wireOp",EDGE,"E97"),sQuery(id+"F2.wireOp",EDGE,"E98"),sQuery(id+"F2.wireOp",EDGE,"E99"),sQuery(id+"F2.wireOp",EDGE,"E100"),sQuery(id+"F2.wireOp",EDGE,"E101"),sQuery(id+"F2.wireOp",EDGE,"E102"),sQuery(id+"F2.wireOp",EDGE,"E134"),sQuery(id+"F2.wireOp",EDGE,"E135"),sQuery(id+"F2.wireOp",EDGE,"E136"),sQuery(id+"F2.wireOp",EDGE,"E137"),sQuery(id+"F2.wireOp",EDGE,"E139"),sQuery(id+"F2.wireOp",EDGE,"E141"),sQuery(id+"F2.wireOp",EDGE,"E142"),sQuery(id+"F2.wireOp",EDGE,"E143"),sQuery(id+"F2.wireOp",EDGE,"E144"),sQuery(id+"F2.wireOp",EDGE,"E145"),sQuery(id+"F2.wireOp",EDGE,"E146"),sQuery(id+"F2.wireOp",EDGE,"E147"),sQuery(id+"F2.wireOp",EDGE,"E148")])],"isStart":false});
            var Q6;
            Q6=makeQuery(id+"F3.opExtrude","CAP_FACE",FACE,{"disambiguationData":[OSD([sQuery(id+"F2.wireOp",EDGE,"E28"),sQuery(id+"F2.wireOp",EDGE,"E29"),sQuery(id+"F2.wireOp",EDGE,"E30")])],"isStart":false});
            var Q7;
            Q7=makeQuery(id+"F3.opExtrude","CAP_FACE",FACE,{"disambiguationData":[OSD([sQuery(id+"F2.wireOp",EDGE,"E33"),sQuery(id+"F2.wireOp",EDGE,"E34"),sQuery(id+"F2.wireOp",EDGE,"E42.trimOffspring")])],"isStart":false});
            var Q8;
            Q8=makeQuery(id+"F3.opExtrude","CAP_FACE",FACE,{"disambiguationData":[OSD([sQuery(id+"F2.wireOp",EDGE,"E31"),sQuery(id+"F2.wireOp",EDGE,"E32"),sQuery(id+"F2.wireOp",EDGE,"E41.trimOffspring")])],"isStart":false});
            var Q9;
            Q9=makeQuery(id+"F3.opExtrude","CAP_FACE",FACE,{"disambiguationData":[OSD([sQuery(id+"F2.wireOp",EDGE,"E52"),sQuery(id+"F2.wireOp",EDGE,"E53"),sQuery(id+"F2.wireOp",EDGE,"E54"),sQuery(id+"F2.wireOp",EDGE,"E55")])],"isStart":false});
            var Q10;
            Q10=makeQuery(id+"F3.opExtrude","CAP_FACE",FACE,{"disambiguationData":[OSD([sQuery(id+"F2.wireOp",EDGE,"E61"),sQuery(id+"F2.wireOp",EDGE,"E62"),sQuery(id+"F2.wireOp",EDGE,"E63"),sQuery(id+"F2.wireOp",EDGE,"E64"),sQuery(id+"F2.wireOp",EDGE,"E138"),sQuery(id+"F2.wireOp",EDGE,"E140"),sQuery(id+"F2.wireOp",EDGE,"E149"),sQuery(id+"F2.wireOp",EDGE,"E150"),sQuery(id+"F2.wireOp",EDGE,"E151"),sQuery(id+"F2.wireOp",EDGE,"E152"),sQuery(id+"F2.wireOp",EDGE,"E153")])],"isStart":false});
            var Q11;
            Q11=makeQuery(id+"F3.opExtrude","CAP_FACE",FACE,{"disambiguationData":[OSD([sQuery(id+"F2.wireOp",EDGE,"E48"),sQuery(id+"F2.wireOp",EDGE,"E49"),sQuery(id+"F2.wireOp",EDGE,"E50"),sQuery(id+"F2.wireOp",EDGE,"E51")])],"isStart":false});
            var Q12;
            Q12=makeQuery(id+"F3.opExtrude","CAP_FACE",FACE,{"disambiguationData":[OSD([sQuery(id+"F2.wireOp",EDGE,"E157"),sQuery(id+"F2.wireOp",EDGE,"E158"),sQuery(id+"F2.wireOp",EDGE,"E159")])],"isStart":false});
            var Q13;
            Q13=makeQuery(id+"F3.opExtrude","CAP_FACE",FACE,{"disambiguationData":[OSD([sQuery(id+"F2.wireOp",EDGE,"E65"),sQuery(id+"F2.wireOp",EDGE,"E66"),sQuery(id+"F2.wireOp",EDGE,"E67"),sQuery(id+"F2.wireOp",EDGE,"E68"),sQuery(id+"F2.wireOp",EDGE,"E69"),sQuery(id+"F2.wireOp",EDGE,"E70"),sQuery(id+"F2.wireOp",EDGE,"E71"),sQuery(id+"F2.wireOp",EDGE,"E72"),sQuery(id+"F2.wireOp",EDGE,"E73"),sQuery(id+"F2.wireOp",EDGE,"E74"),sQuery(id+"F2.wireOp",EDGE,"E75"),sQuery(id+"F2.wireOp",EDGE,"E76"),sQuery(id+"F2.wireOp",EDGE,"E77"),sQuery(id+"F2.wireOp",EDGE,"E78"),sQuery(id+"F2.wireOp",EDGE,"E79"),sQuery(id+"F2.wireOp",EDGE,"E80"),sQuery(id+"F2.wireOp",EDGE,"E103"),sQuery(id+"F2.wireOp",EDGE,"E108"),sQuery(id+"F2.wireOp",EDGE,"E112"),sQuery(id+"F2.wireOp",EDGE,"E113"),sQuery(id+"F2.wireOp",EDGE,"E114"),sQuery(id+"F2.wireOp",EDGE,"E161"),sQuery(id+"F2.wireOp",EDGE,"E162")])],"isStart":false});
            var Q14;
            Q14=makeQuery(id+"F3.opExtrude","CAP_FACE",FACE,{"disambiguationData":[OSD([sQuery(id+"F2.wireOp",EDGE,"E92"),sQuery(id+"F2.wireOp",EDGE,"E93"),sQuery(id+"F2.wireOp",EDGE,"E94"),sQuery(id+"F2.wireOp",EDGE,"E95"),sQuery(id+"F2.wireOp",EDGE,"E96"),sQuery(id+"F2.wireOp",EDGE,"E115"),sQuery(id+"F2.wireOp",EDGE,"E116"),sQuery(id+"F2.wireOp",EDGE,"E117"),sQuery(id+"F2.wireOp",EDGE,"E118"),sQuery(id+"F2.wireOp",EDGE,"E119"),sQuery(id+"F2.wireOp",EDGE,"E120"),sQuery(id+"F2.wireOp",EDGE,"E121"),sQuery(id+"F2.wireOp",EDGE,"E122"),sQuery(id+"F2.wireOp",EDGE,"E123"),sQuery(id+"F2.wireOp",EDGE,"E124"),sQuery(id+"F2.wireOp",EDGE,"E125"),sQuery(id+"F2.wireOp",EDGE,"E126"),sQuery(id+"F2.wireOp",EDGE,"E127"),sQuery(id+"F2.wireOp",EDGE,"E128"),sQuery(id+"F2.wireOp",EDGE,"E129"),sQuery(id+"F2.wireOp",EDGE,"E130"),sQuery(id+"F2.wireOp",EDGE,"E131"),sQuery(id+"F2.wireOp",EDGE,"E132"),sQuery(id+"F2.wireOp",EDGE,"E133")])],"isStart":false});
            var Q15;
            Q15=makeQuery(id+"F3.opExtrude","CAP_FACE",FACE,{"disambiguationData":[OSD([sQuery(id+"F2.wireOp",EDGE,"E8"),sQuery(id+"F2.wireOp",EDGE,"E9"),sQuery(id+"F2.wireOp",EDGE,"E10"),sQuery(id+"F2.wireOp",EDGE,"E11"),sQuery(id+"F2.wireOp",EDGE,"E12"),sQuery(id+"F2.wireOp",EDGE,"E13"),sQuery(id+"F2.wireOp",EDGE,"E14")])],"isStart":false});
            var Q16;
            Q16=makeQuery(id+"F3.opExtrude","CAP_FACE",FACE,{"disambiguationData":[OSD([sQuery(id+"F2.wireOp",EDGE,"E88"),sQuery(id+"F2.wireOp",EDGE,"E89"),sQuery(id+"F2.wireOp",EDGE,"E90"),sQuery(id+"F2.wireOp",EDGE,"E91")])],"isStart":false});
            var Q17;
            Q17=makeQuery(id+"F3.opExtrude","CAP_FACE",FACE,{"disambiguationData":[OSD([sQuery(id+"F2.wireOp",EDGE,"E24"),sQuery(id+"F2.wireOp",EDGE,"E25"),sQuery(id+"F2.wireOp",EDGE,"E26"),sQuery(id+"F2.wireOp",EDGE,"E27")])],"isStart":false});
            var Q18;
            Q18=makeQuery(id+"F3.opExtrude","CAP_FACE",FACE,{"disambiguationData":[OSD([sQuery(id+"F2.wireOp",EDGE,"E81"),sQuery(id+"F2.wireOp",EDGE,"E82"),sQuery(id+"F2.wireOp",EDGE,"E83"),sQuery(id+"F2.wireOp",EDGE,"E84"),sQuery(id+"F2.wireOp",EDGE,"E85"),sQuery(id+"F2.wireOp",EDGE,"E86"),sQuery(id+"F2.wireOp",EDGE,"E87")])],"isStart":false});
            var Q19;
            Q19=makeQuery(id+"F3.opExtrude","CAP_FACE",FACE,{"disambiguationData":[OSD([sQuery(id+"F2.wireOp",EDGE,"E163"),sQuery(id+"F2.wireOp",EDGE,"E172"),sQuery(id+"F2.wireOp",EDGE,"E173")])],"isStart":false});
            var Q20;
            Q20=makeQuery(id+"F3.opExtrude","CAP_FACE",FACE,{"disambiguationData":[OSD([sQuery(id+"F2.wireOp",EDGE,"E164"),sQuery(id+"F2.wireOp",EDGE,"E165"),sQuery(id+"F2.wireOp",EDGE,"E177.trimOffspring")])],"isStart":false});
            var Q21;
            Q21=makeQuery(id+"F3.opExtrude","CAP_FACE",FACE,{"disambiguationData":[OSD([sQuery(id+"F2.wireOp",EDGE,"E166"),sQuery(id+"F2.wireOp",EDGE,"E167"),sQuery(id+"F2.wireOp",EDGE,"E176.trimOffspring")])],"isStart":false});
            var Q22;
            Q22=makeQuery(id+"F3.opExtrude","CAP_FACE",FACE,{"disambiguationData":[OSD([sQuery(id+"F2.wireOp",EDGE,"E168"),sQuery(id+"F2.wireOp",EDGE,"E169"),sQuery(id+"F2.wireOp",EDGE,"E175.trimOffspring")])],"isStart":false});
            var Q23;
            Q23=makeQuery(id+"F3.opExtrude","CAP_FACE",FACE,{"disambiguationData":[OSD([sQuery(id+"F2.wireOp",EDGE,"E170"),sQuery(id+"F2.wireOp",EDGE,"E171"),sQuery(id+"F2.wireOp",EDGE,"E174.trimOffspring")])],"isStart":false});
            var Q24;
            Q24=makeQuery(id+"F3.opExtrude","CAP_FACE",FACE,{"disambiguationData":[OSD([sQuery(id+"F2.wireOp",EDGE,"E154"),sQuery(id+"F2.wireOp",EDGE,"E155"),sQuery(id+"F2.wireOp",EDGE,"E156")])],"isStart":false});
            var Q25;
            Q25=makeQuery(id+"F3.opExtrude","CAP_FACE",FACE,{"disambiguationData":[OSD([sQuery(id+"F2.wireOp",EDGE,"E43"),sQuery(id+"F2.wireOp",EDGE,"E44"),sQuery(id+"F2.wireOp",EDGE,"E45"),sQuery(id+"F2.wireOp",EDGE,"E46"),sQuery(id+"F2.wireOp",EDGE,"E47")])],"isStart":false});
            var Q26;
            Q26=makeQuery(id+"F3.opExtrude","CAP_FACE",FACE,{"disambiguationData":[OSD([sQuery(id+"F2.wireOp",EDGE,"E160")])],"isStart":false});
            extrude(context, id + "F18", {"entities" : qUnion([Q0, Q1, Q2, Q3, Q4, Q5, Q6, Q7, Q8, Q9, Q10, Q11, Q12, Q13, Q14, Q15, Q16, Q17, Q18, Q19, Q20, Q21, Q22, Q23, Q24, Q25, Q26]), "operationType" : NewBodyOperationType.ADD, "depth" : 0.5 * mm});
        }
        {
            var Q0;
            Q0=makeQuery(id+"F9.opExtrude","CAP_FACE",FACE,{"disambiguationData":[OSD([sQuery(id+"F8.wireOp",EDGE,"E195.sketch_text.stroke-0"),sQuery(id+"F8.wireOp",EDGE,"E195.sketch_text.stroke-1"),sQuery(id+"F8.wireOp",EDGE,"E195.sketch_text.stroke-2"),sQuery(id+"F8.wireOp",EDGE,"E195.sketch_text.stroke-3"),sQuery(id+"F8.wireOp",EDGE,"E195.sketch_text.stroke-4"),sQuery(id+"F8.wireOp",EDGE,"E195.sketch_text.stroke-5"),sQuery(id+"F8.wireOp",EDGE,"E195.sketch_text.stroke-6"),sQuery(id+"F8.wireOp",EDGE,"E195.sketch_text.stroke-7"),sQuery(id+"F8.wireOp",EDGE,"E195.sketch_text.stroke-8"),sQuery(id+"F8.wireOp",EDGE,"E195.sketch_text.stroke-9"),sQuery(id+"F8.wireOp",EDGE,"E195.sketch_text.stroke-10"),sQuery(id+"F8.wireOp",EDGE,"E195.sketch_text.stroke-11"),sQuery(id+"F8.wireOp",EDGE,"E195.sketch_text.stroke-12"),sQuery(id+"F8.wireOp",EDGE,"E195.sketch_text.stroke-13"),sQuery(id+"F8.wireOp",EDGE,"E195.sketch_text.stroke-14"),sQuery(id+"F8.wireOp",EDGE,"E195.sketch_text.stroke-15"),sQuery(id+"F8.wireOp",EDGE,"E195.sketch_text.stroke-16"),sQuery(id+"F8.wireOp",EDGE,"E195.sketch_text.stroke-17"),sQuery(id+"F8.wireOp",EDGE,"E195.sketch_text.stroke-18"),sQuery(id+"F8.wireOp",EDGE,"E195.sketch_text.stroke-19"),sQuery(id+"F8.wireOp",EDGE,"E195.sketch_text.stroke-20"),sQuery(id+"F8.wireOp",EDGE,"E195.sketch_text.stroke-21"),sQuery(id+"F8.wireOp",EDGE,"E195.sketch_text.stroke-22"),sQuery(id+"F8.wireOp",EDGE,"E195.sketch_text.stroke-23"),sQuery(id+"F8.wireOp",EDGE,"E195.sketch_text.stroke-24"),sQuery(id+"F8.wireOp",EDGE,"E195.sketch_text.stroke-25")])],"isStart":false});
            var Q1;
            Q1=makeQuery(id+"F9.opExtrude","CAP_FACE",FACE,{"disambiguationData":[OSD([sQuery(id+"F8.wireOp",EDGE,"E195.sketch_text.stroke-26"),sQuery(id+"F8.wireOp",EDGE,"E195.sketch_text.stroke-27"),sQuery(id+"F8.wireOp",EDGE,"E195.sketch_text.stroke-28"),sQuery(id+"F8.wireOp",EDGE,"E195.sketch_text.stroke-29"),sQuery(id+"F8.wireOp",EDGE,"E195.sketch_text.stroke-30"),sQuery(id+"F8.wireOp",EDGE,"E195.sketch_text.stroke-31"),sQuery(id+"F8.wireOp",EDGE,"E195.sketch_text.stroke-32"),sQuery(id+"F8.wireOp",EDGE,"E195.sketch_text.stroke-33"),sQuery(id+"F8.wireOp",EDGE,"E195.sketch_text.stroke-34"),sQuery(id+"F8.wireOp",EDGE,"E195.sketch_text.stroke-35"),sQuery(id+"F8.wireOp",EDGE,"E195.sketch_text.stroke-36"),sQuery(id+"F8.wireOp",EDGE,"E195.sketch_text.stroke-37"),sQuery(id+"F8.wireOp",EDGE,"E195.sketch_text.stroke-38"),sQuery(id+"F8.wireOp",EDGE,"E195.sketch_text.stroke-39"),sQuery(id+"F8.wireOp",EDGE,"E195.sketch_text.stroke-40"),sQuery(id+"F8.wireOp",EDGE,"E195.sketch_text.stroke-41"),sQuery(id+"F8.wireOp",EDGE,"E195.sketch_text.stroke-42"),sQuery(id+"F8.wireOp",EDGE,"E195.sketch_text.stroke-43"),sQuery(id+"F8.wireOp",EDGE,"E195.sketch_text.stroke-44"),sQuery(id+"F8.wireOp",EDGE,"E195.sketch_text.stroke-45"),sQuery(id+"F8.wireOp",EDGE,"E195.sketch_text.stroke-46"),sQuery(id+"F8.wireOp",EDGE,"E195.sketch_text.stroke-47"),sQuery(id+"F8.wireOp",EDGE,"E195.sketch_text.stroke-48"),sQuery(id+"F8.wireOp",EDGE,"E195.sketch_text.stroke-49"),sQuery(id+"F8.wireOp",EDGE,"E195.sketch_text.stroke-50"),sQuery(id+"F8.wireOp",EDGE,"E195.sketch_text.stroke-51"),sQuery(id+"F8.wireOp",EDGE,"E195.sketch_text.stroke-52"),sQuery(id+"F8.wireOp",EDGE,"E195.sketch_text.stroke-53"),sQuery(id+"F8.wireOp",EDGE,"E195.sketch_text.stroke-54"),sQuery(id+"F8.wireOp",EDGE,"E195.sketch_text.stroke-55"),sQuery(id+"F8.wireOp",EDGE,"E195.sketch_text.stroke-56"),sQuery(id+"F8.wireOp",EDGE,"E195.sketch_text.stroke-57"),sQuery(id+"F8.wireOp",EDGE,"E195.sketch_text.stroke-58"),sQuery(id+"F8.wireOp",EDGE,"E195.sketch_text.stroke-59"),sQuery(id+"F8.wireOp",EDGE,"E195.sketch_text.stroke-60"),sQuery(id+"F8.wireOp",EDGE,"E195.sketch_text.stroke-61")])],"isStart":false});
            var Q2;
            Q2=makeQuery(id+"F9.opExtrude","CAP_FACE",FACE,{"disambiguationData":[OSD([sQuery(id+"F8.wireOp",EDGE,"E195.sketch_text.stroke-62"),sQuery(id+"F8.wireOp",EDGE,"E195.sketch_text.stroke-63"),sQuery(id+"F8.wireOp",EDGE,"E195.sketch_text.stroke-64"),sQuery(id+"F8.wireOp",EDGE,"E195.sketch_text.stroke-65"),sQuery(id+"F8.wireOp",EDGE,"E195.sketch_text.stroke-66"),sQuery(id+"F8.wireOp",EDGE,"E195.sketch_text.stroke-67"),sQuery(id+"F8.wireOp",EDGE,"E195.sketch_text.stroke-68"),sQuery(id+"F8.wireOp",EDGE,"E195.sketch_text.stroke-69"),sQuery(id+"F8.wireOp",EDGE,"E195.sketch_text.stroke-70"),sQuery(id+"F8.wireOp",EDGE,"E195.sketch_text.stroke-71"),sQuery(id+"F8.wireOp",EDGE,"E195.sketch_text.stroke-72"),sQuery(id+"F8.wireOp",EDGE,"E195.sketch_text.stroke-73"),sQuery(id+"F8.wireOp",EDGE,"E195.sketch_text.stroke-74"),sQuery(id+"F8.wireOp",EDGE,"E195.sketch_text.stroke-75"),sQuery(id+"F8.wireOp",EDGE,"E195.sketch_text.stroke-76"),sQuery(id+"F8.wireOp",EDGE,"E195.sketch_text.stroke-77"),sQuery(id+"F8.wireOp",EDGE,"E195.sketch_text.stroke-78"),sQuery(id+"F8.wireOp",EDGE,"E195.sketch_text.stroke-79"),sQuery(id+"F8.wireOp",EDGE,"E195.sketch_text.stroke-80"),sQuery(id+"F8.wireOp",EDGE,"E195.sketch_text.stroke-81")])],"isStart":false});
            var Q3;
            Q3=makeQuery(id+"F9.opExtrude","CAP_FACE",FACE,{"disambiguationData":[OSD([sQuery(id+"F8.wireOp",EDGE,"E195.sketch_text.stroke-82"),sQuery(id+"F8.wireOp",EDGE,"E195.sketch_text.stroke-83"),sQuery(id+"F8.wireOp",EDGE,"E195.sketch_text.stroke-84"),sQuery(id+"F8.wireOp",EDGE,"E195.sketch_text.stroke-85"),sQuery(id+"F8.wireOp",EDGE,"E195.sketch_text.stroke-86"),sQuery(id+"F8.wireOp",EDGE,"E195.sketch_text.stroke-87"),sQuery(id+"F8.wireOp",EDGE,"E195.sketch_text.stroke-88"),sQuery(id+"F8.wireOp",EDGE,"E195.sketch_text.stroke-89"),sQuery(id+"F8.wireOp",EDGE,"E195.sketch_text.stroke-90"),sQuery(id+"F8.wireOp",EDGE,"E195.sketch_text.stroke-91"),sQuery(id+"F8.wireOp",EDGE,"E195.sketch_text.stroke-92"),sQuery(id+"F8.wireOp",EDGE,"E195.sketch_text.stroke-93"),sQuery(id+"F8.wireOp",EDGE,"E195.sketch_text.stroke-94"),sQuery(id+"F8.wireOp",EDGE,"E195.sketch_text.stroke-95"),sQuery(id+"F8.wireOp",EDGE,"E195.sketch_text.stroke-96"),sQuery(id+"F8.wireOp",EDGE,"E195.sketch_text.stroke-97"),sQuery(id+"F8.wireOp",EDGE,"E195.sketch_text.stroke-98"),sQuery(id+"F8.wireOp",EDGE,"E195.sketch_text.stroke-99"),sQuery(id+"F8.wireOp",EDGE,"E195.sketch_text.stroke-100"),sQuery(id+"F8.wireOp",EDGE,"E195.sketch_text.stroke-101"),sQuery(id+"F8.wireOp",EDGE,"E195.sketch_text.stroke-102"),sQuery(id+"F8.wireOp",EDGE,"E195.sketch_text.stroke-103"),sQuery(id+"F8.wireOp",EDGE,"E195.sketch_text.stroke-104"),sQuery(id+"F8.wireOp",EDGE,"E195.sketch_text.stroke-105")])],"isStart":false});
            var Q4;
            Q4=makeQuery(id+"F9.opExtrude","CAP_FACE",FACE,{"disambiguationData":[OSD([sQuery(id+"F8.wireOp",EDGE,"E195.sketch_text.stroke-106"),sQuery(id+"F8.wireOp",EDGE,"E195.sketch_text.stroke-107"),sQuery(id+"F8.wireOp",EDGE,"E195.sketch_text.stroke-108"),sQuery(id+"F8.wireOp",EDGE,"E195.sketch_text.stroke-109"),sQuery(id+"F8.wireOp",EDGE,"E195.sketch_text.stroke-110"),sQuery(id+"F8.wireOp",EDGE,"E195.sketch_text.stroke-111"),sQuery(id+"F8.wireOp",EDGE,"E195.sketch_text.stroke-112"),sQuery(id+"F8.wireOp",EDGE,"E195.sketch_text.stroke-113"),sQuery(id+"F8.wireOp",EDGE,"E195.sketch_text.stroke-114"),sQuery(id+"F8.wireOp",EDGE,"E195.sketch_text.stroke-115"),sQuery(id+"F8.wireOp",EDGE,"E195.sketch_text.stroke-116"),sQuery(id+"F8.wireOp",EDGE,"E195.sketch_text.stroke-117"),sQuery(id+"F8.wireOp",EDGE,"E195.sketch_text.stroke-118"),sQuery(id+"F8.wireOp",EDGE,"E195.sketch_text.stroke-119"),sQuery(id+"F8.wireOp",EDGE,"E195.sketch_text.stroke-120"),sQuery(id+"F8.wireOp",EDGE,"E195.sketch_text.stroke-121"),sQuery(id+"F8.wireOp",EDGE,"E195.sketch_text.stroke-122"),sQuery(id+"F8.wireOp",EDGE,"E195.sketch_text.stroke-123"),sQuery(id+"F8.wireOp",EDGE,"E195.sketch_text.stroke-124"),sQuery(id+"F8.wireOp",EDGE,"E195.sketch_text.stroke-125"),sQuery(id+"F8.wireOp",EDGE,"E195.sketch_text.stroke-126")])],"isStart":false});
            var Q5;
            Q5=makeQuery(id+"F9.opExtrude","CAP_FACE",FACE,{"disambiguationData":[OSD([sQuery(id+"F8.wireOp",EDGE,"E196.sketch_text.stroke-160"),sQuery(id+"F8.wireOp",EDGE,"E196.sketch_text.stroke-161"),sQuery(id+"F8.wireOp",EDGE,"E196.sketch_text.stroke-162"),sQuery(id+"F8.wireOp",EDGE,"E196.sketch_text.stroke-163"),sQuery(id+"F8.wireOp",EDGE,"E196.sketch_text.stroke-164"),sQuery(id+"F8.wireOp",EDGE,"E196.sketch_text.stroke-165"),sQuery(id+"F8.wireOp",EDGE,"E196.sketch_text.stroke-166"),sQuery(id+"F8.wireOp",EDGE,"E196.sketch_text.stroke-167"),sQuery(id+"F8.wireOp",EDGE,"E196.sketch_text.stroke-168"),sQuery(id+"F8.wireOp",EDGE,"E196.sketch_text.stroke-169"),sQuery(id+"F8.wireOp",EDGE,"E196.sketch_text.stroke-170"),sQuery(id+"F8.wireOp",EDGE,"E196.sketch_text.stroke-171"),sQuery(id+"F8.wireOp",EDGE,"E196.sketch_text.stroke-172"),sQuery(id+"F8.wireOp",EDGE,"E196.sketch_text.stroke-173"),sQuery(id+"F8.wireOp",EDGE,"E196.sketch_text.stroke-174"),sQuery(id+"F8.wireOp",EDGE,"E196.sketch_text.stroke-175"),sQuery(id+"F8.wireOp",EDGE,"E196.sketch_text.stroke-176"),sQuery(id+"F8.wireOp",EDGE,"E196.sketch_text.stroke-177"),sQuery(id+"F8.wireOp",EDGE,"E196.sketch_text.stroke-178"),sQuery(id+"F8.wireOp",EDGE,"E196.sketch_text.stroke-179"),sQuery(id+"F8.wireOp",EDGE,"E196.sketch_text.stroke-180"),sQuery(id+"F8.wireOp",EDGE,"E196.sketch_text.stroke-181"),sQuery(id+"F8.wireOp",EDGE,"E196.sketch_text.stroke-182"),sQuery(id+"F8.wireOp",EDGE,"E196.sketch_text.stroke-183")])],"isStart":false});
            var Q6;
            Q6=makeQuery(id+"F9.opExtrude","CAP_FACE",FACE,{"disambiguationData":[OSD([sQuery(id+"F8.wireOp",EDGE,"E196.sketch_text.stroke-140"),sQuery(id+"F8.wireOp",EDGE,"E196.sketch_text.stroke-141"),sQuery(id+"F8.wireOp",EDGE,"E196.sketch_text.stroke-142"),sQuery(id+"F8.wireOp",EDGE,"E196.sketch_text.stroke-143"),sQuery(id+"F8.wireOp",EDGE,"E196.sketch_text.stroke-144"),sQuery(id+"F8.wireOp",EDGE,"E196.sketch_text.stroke-145"),sQuery(id+"F8.wireOp",EDGE,"E196.sketch_text.stroke-146"),sQuery(id+"F8.wireOp",EDGE,"E196.sketch_text.stroke-147"),sQuery(id+"F8.wireOp",EDGE,"E196.sketch_text.stroke-148"),sQuery(id+"F8.wireOp",EDGE,"E196.sketch_text.stroke-149"),sQuery(id+"F8.wireOp",EDGE,"E196.sketch_text.stroke-150"),sQuery(id+"F8.wireOp",EDGE,"E196.sketch_text.stroke-151"),sQuery(id+"F8.wireOp",EDGE,"E196.sketch_text.stroke-152"),sQuery(id+"F8.wireOp",EDGE,"E196.sketch_text.stroke-153"),sQuery(id+"F8.wireOp",EDGE,"E196.sketch_text.stroke-154"),sQuery(id+"F8.wireOp",EDGE,"E196.sketch_text.stroke-155"),sQuery(id+"F8.wireOp",EDGE,"E196.sketch_text.stroke-156"),sQuery(id+"F8.wireOp",EDGE,"E196.sketch_text.stroke-157"),sQuery(id+"F8.wireOp",EDGE,"E196.sketch_text.stroke-158"),sQuery(id+"F8.wireOp",EDGE,"E196.sketch_text.stroke-159")])],"isStart":false});
            var Q7;
            Q7=makeQuery(id+"F9.opExtrude","CAP_FACE",FACE,{"disambiguationData":[OSD([sQuery(id+"F8.wireOp",EDGE,"E196.sketch_text.stroke-128"),sQuery(id+"F8.wireOp",EDGE,"E196.sketch_text.stroke-129"),sQuery(id+"F8.wireOp",EDGE,"E196.sketch_text.stroke-130"),sQuery(id+"F8.wireOp",EDGE,"E196.sketch_text.stroke-131"),sQuery(id+"F8.wireOp",EDGE,"E196.sketch_text.stroke-132"),sQuery(id+"F8.wireOp",EDGE,"E196.sketch_text.stroke-133"),sQuery(id+"F8.wireOp",EDGE,"E196.sketch_text.stroke-134"),sQuery(id+"F8.wireOp",EDGE,"E196.sketch_text.stroke-135"),sQuery(id+"F8.wireOp",EDGE,"E196.sketch_text.stroke-136"),sQuery(id+"F8.wireOp",EDGE,"E196.sketch_text.stroke-137"),sQuery(id+"F8.wireOp",EDGE,"E196.sketch_text.stroke-138"),sQuery(id+"F8.wireOp",EDGE,"E196.sketch_text.stroke-139")])],"isStart":false});
            var Q8;
            Q8=makeQuery(id+"F9.opExtrude","CAP_FACE",FACE,{"disambiguationData":[OSD([sQuery(id+"F8.wireOp",EDGE,"E196.sketch_text.stroke-105"),sQuery(id+"F8.wireOp",EDGE,"E196.sketch_text.stroke-106"),sQuery(id+"F8.wireOp",EDGE,"E196.sketch_text.stroke-107"),sQuery(id+"F8.wireOp",EDGE,"E196.sketch_text.stroke-108"),sQuery(id+"F8.wireOp",EDGE,"E196.sketch_text.stroke-109"),sQuery(id+"F8.wireOp",EDGE,"E196.sketch_text.stroke-110"),sQuery(id+"F8.wireOp",EDGE,"E196.sketch_text.stroke-111"),sQuery(id+"F8.wireOp",EDGE,"E196.sketch_text.stroke-112"),sQuery(id+"F8.wireOp",EDGE,"E196.sketch_text.stroke-113"),sQuery(id+"F8.wireOp",EDGE,"E196.sketch_text.stroke-114"),sQuery(id+"F8.wireOp",EDGE,"E196.sketch_text.stroke-115"),sQuery(id+"F8.wireOp",EDGE,"E196.sketch_text.stroke-116"),sQuery(id+"F8.wireOp",EDGE,"E196.sketch_text.stroke-117"),sQuery(id+"F8.wireOp",EDGE,"E196.sketch_text.stroke-118"),sQuery(id+"F8.wireOp",EDGE,"E196.sketch_text.stroke-119"),sQuery(id+"F8.wireOp",EDGE,"E196.sketch_text.stroke-120"),sQuery(id+"F8.wireOp",EDGE,"E196.sketch_text.stroke-121"),sQuery(id+"F8.wireOp",EDGE,"E196.sketch_text.stroke-122"),sQuery(id+"F8.wireOp",EDGE,"E196.sketch_text.stroke-123"),sQuery(id+"F8.wireOp",EDGE,"E196.sketch_text.stroke-124"),sQuery(id+"F8.wireOp",EDGE,"E196.sketch_text.stroke-125"),sQuery(id+"F8.wireOp",EDGE,"E196.sketch_text.stroke-126"),sQuery(id+"F8.wireOp",EDGE,"E196.sketch_text.stroke-127")])],"isStart":false});
            var Q9;
            Q9=makeQuery(id+"F9.opExtrude","CAP_FACE",FACE,{"disambiguationData":[OSD([sQuery(id+"F8.wireOp",EDGE,"E196.sketch_text.stroke-74"),sQuery(id+"F8.wireOp",EDGE,"E196.sketch_text.stroke-75"),sQuery(id+"F8.wireOp",EDGE,"E196.sketch_text.stroke-76"),sQuery(id+"F8.wireOp",EDGE,"E196.sketch_text.stroke-77"),sQuery(id+"F8.wireOp",EDGE,"E196.sketch_text.stroke-78"),sQuery(id+"F8.wireOp",EDGE,"E196.sketch_text.stroke-79"),sQuery(id+"F8.wireOp",EDGE,"E196.sketch_text.stroke-80"),sQuery(id+"F8.wireOp",EDGE,"E196.sketch_text.stroke-81"),sQuery(id+"F8.wireOp",EDGE,"E196.sketch_text.stroke-82"),sQuery(id+"F8.wireOp",EDGE,"E196.sketch_text.stroke-83"),sQuery(id+"F8.wireOp",EDGE,"E196.sketch_text.stroke-84"),sQuery(id+"F8.wireOp",EDGE,"E196.sketch_text.stroke-85"),sQuery(id+"F8.wireOp",EDGE,"E196.sketch_text.stroke-86"),sQuery(id+"F8.wireOp",EDGE,"E196.sketch_text.stroke-87"),sQuery(id+"F8.wireOp",EDGE,"E196.sketch_text.stroke-88"),sQuery(id+"F8.wireOp",EDGE,"E196.sketch_text.stroke-89"),sQuery(id+"F8.wireOp",EDGE,"E196.sketch_text.stroke-90"),sQuery(id+"F8.wireOp",EDGE,"E196.sketch_text.stroke-91"),sQuery(id+"F8.wireOp",EDGE,"E196.sketch_text.stroke-92"),sQuery(id+"F8.wireOp",EDGE,"E196.sketch_text.stroke-93"),sQuery(id+"F8.wireOp",EDGE,"E196.sketch_text.stroke-94"),sQuery(id+"F8.wireOp",EDGE,"E196.sketch_text.stroke-95"),sQuery(id+"F8.wireOp",EDGE,"E196.sketch_text.stroke-96"),sQuery(id+"F8.wireOp",EDGE,"E196.sketch_text.stroke-97"),sQuery(id+"F8.wireOp",EDGE,"E196.sketch_text.stroke-98"),sQuery(id+"F8.wireOp",EDGE,"E196.sketch_text.stroke-99"),sQuery(id+"F8.wireOp",EDGE,"E196.sketch_text.stroke-100"),sQuery(id+"F8.wireOp",EDGE,"E196.sketch_text.stroke-101"),sQuery(id+"F8.wireOp",EDGE,"E196.sketch_text.stroke-102"),sQuery(id+"F8.wireOp",EDGE,"E196.sketch_text.stroke-103"),sQuery(id+"F8.wireOp",EDGE,"E196.sketch_text.stroke-104")])],"isStart":false});
            var Q10;
            Q10=makeQuery(id+"F9.opExtrude","CAP_FACE",FACE,{"disambiguationData":[OSD([sQuery(id+"F8.wireOp",EDGE,"E196.sketch_text.stroke-54"),sQuery(id+"F8.wireOp",EDGE,"E196.sketch_text.stroke-55"),sQuery(id+"F8.wireOp",EDGE,"E196.sketch_text.stroke-56"),sQuery(id+"F8.wireOp",EDGE,"E196.sketch_text.stroke-57"),sQuery(id+"F8.wireOp",EDGE,"E196.sketch_text.stroke-58"),sQuery(id+"F8.wireOp",EDGE,"E196.sketch_text.stroke-59"),sQuery(id+"F8.wireOp",EDGE,"E196.sketch_text.stroke-60"),sQuery(id+"F8.wireOp",EDGE,"E196.sketch_text.stroke-61"),sQuery(id+"F8.wireOp",EDGE,"E196.sketch_text.stroke-62"),sQuery(id+"F8.wireOp",EDGE,"E196.sketch_text.stroke-63"),sQuery(id+"F8.wireOp",EDGE,"E196.sketch_text.stroke-64"),sQuery(id+"F8.wireOp",EDGE,"E196.sketch_text.stroke-65"),sQuery(id+"F8.wireOp",EDGE,"E196.sketch_text.stroke-66"),sQuery(id+"F8.wireOp",EDGE,"E196.sketch_text.stroke-67"),sQuery(id+"F8.wireOp",EDGE,"E196.sketch_text.stroke-68"),sQuery(id+"F8.wireOp",EDGE,"E196.sketch_text.stroke-69"),sQuery(id+"F8.wireOp",EDGE,"E196.sketch_text.stroke-70"),sQuery(id+"F8.wireOp",EDGE,"E196.sketch_text.stroke-71"),sQuery(id+"F8.wireOp",EDGE,"E196.sketch_text.stroke-72"),sQuery(id+"F8.wireOp",EDGE,"E196.sketch_text.stroke-73")])],"isStart":false});
            var Q11;
            Q11=makeQuery(id+"F9.opExtrude","CAP_FACE",FACE,{"disambiguationData":[OSD([sQuery(id+"F8.wireOp",EDGE,"E196.sketch_text.stroke-24"),sQuery(id+"F8.wireOp",EDGE,"E196.sketch_text.stroke-25"),sQuery(id+"F8.wireOp",EDGE,"E196.sketch_text.stroke-26"),sQuery(id+"F8.wireOp",EDGE,"E196.sketch_text.stroke-27"),sQuery(id+"F8.wireOp",EDGE,"E196.sketch_text.stroke-28"),sQuery(id+"F8.wireOp",EDGE,"E196.sketch_text.stroke-29"),sQuery(id+"F8.wireOp",EDGE,"E196.sketch_text.stroke-30"),sQuery(id+"F8.wireOp",EDGE,"E196.sketch_text.stroke-31"),sQuery(id+"F8.wireOp",EDGE,"E196.sketch_text.stroke-32"),sQuery(id+"F8.wireOp",EDGE,"E196.sketch_text.stroke-33"),sQuery(id+"F8.wireOp",EDGE,"E196.sketch_text.stroke-34"),sQuery(id+"F8.wireOp",EDGE,"E196.sketch_text.stroke-35"),sQuery(id+"F8.wireOp",EDGE,"E196.sketch_text.stroke-36"),sQuery(id+"F8.wireOp",EDGE,"E196.sketch_text.stroke-37"),sQuery(id+"F8.wireOp",EDGE,"E196.sketch_text.stroke-38"),sQuery(id+"F8.wireOp",EDGE,"E196.sketch_text.stroke-39"),sQuery(id+"F8.wireOp",EDGE,"E196.sketch_text.stroke-40"),sQuery(id+"F8.wireOp",EDGE,"E196.sketch_text.stroke-41"),sQuery(id+"F8.wireOp",EDGE,"E196.sketch_text.stroke-42"),sQuery(id+"F8.wireOp",EDGE,"E196.sketch_text.stroke-43"),sQuery(id+"F8.wireOp",EDGE,"E196.sketch_text.stroke-44"),sQuery(id+"F8.wireOp",EDGE,"E196.sketch_text.stroke-45"),sQuery(id+"F8.wireOp",EDGE,"E196.sketch_text.stroke-46"),sQuery(id+"F8.wireOp",EDGE,"E196.sketch_text.stroke-47"),sQuery(id+"F8.wireOp",EDGE,"E196.sketch_text.stroke-48"),sQuery(id+"F8.wireOp",EDGE,"E196.sketch_text.stroke-49"),sQuery(id+"F8.wireOp",EDGE,"E196.sketch_text.stroke-50"),sQuery(id+"F8.wireOp",EDGE,"E196.sketch_text.stroke-51"),sQuery(id+"F8.wireOp",EDGE,"E196.sketch_text.stroke-52"),sQuery(id+"F8.wireOp",EDGE,"E196.sketch_text.stroke-53")])],"isStart":false});
            var Q12;
            Q12=makeQuery(id+"F9.opExtrude","CAP_FACE",FACE,{"disambiguationData":[OSD([sQuery(id+"F8.wireOp",EDGE,"E196.sketch_text.stroke-0"),sQuery(id+"F8.wireOp",EDGE,"E196.sketch_text.stroke-1"),sQuery(id+"F8.wireOp",EDGE,"E196.sketch_text.stroke-2"),sQuery(id+"F8.wireOp",EDGE,"E196.sketch_text.stroke-3"),sQuery(id+"F8.wireOp",EDGE,"E196.sketch_text.stroke-4"),sQuery(id+"F8.wireOp",EDGE,"E196.sketch_text.stroke-5"),sQuery(id+"F8.wireOp",EDGE,"E196.sketch_text.stroke-6"),sQuery(id+"F8.wireOp",EDGE,"E196.sketch_text.stroke-7"),sQuery(id+"F8.wireOp",EDGE,"E196.sketch_text.stroke-8"),sQuery(id+"F8.wireOp",EDGE,"E196.sketch_text.stroke-9"),sQuery(id+"F8.wireOp",EDGE,"E196.sketch_text.stroke-10"),sQuery(id+"F8.wireOp",EDGE,"E196.sketch_text.stroke-11"),sQuery(id+"F8.wireOp",EDGE,"E196.sketch_text.stroke-12"),sQuery(id+"F8.wireOp",EDGE,"E196.sketch_text.stroke-13"),sQuery(id+"F8.wireOp",EDGE,"E196.sketch_text.stroke-14"),sQuery(id+"F8.wireOp",EDGE,"E196.sketch_text.stroke-15"),sQuery(id+"F8.wireOp",EDGE,"E196.sketch_text.stroke-16"),sQuery(id+"F8.wireOp",EDGE,"E196.sketch_text.stroke-17"),sQuery(id+"F8.wireOp",EDGE,"E196.sketch_text.stroke-18"),sQuery(id+"F8.wireOp",EDGE,"E196.sketch_text.stroke-19"),sQuery(id+"F8.wireOp",EDGE,"E196.sketch_text.stroke-20"),sQuery(id+"F8.wireOp",EDGE,"E196.sketch_text.stroke-21"),sQuery(id+"F8.wireOp",EDGE,"E196.sketch_text.stroke-22"),sQuery(id+"F8.wireOp",EDGE,"E196.sketch_text.stroke-23")])],"isStart":false});
            var Q13;
            Q13=makeQuery(id+"F9.opExtrude","CAP_FACE",FACE,{"disambiguationData":[OSD([sQuery(id+"F8.wireOp",EDGE,"E194.sketch_text.stroke-188"),sQuery(id+"F8.wireOp",EDGE,"E194.sketch_text.stroke-189"),sQuery(id+"F8.wireOp",EDGE,"E194.sketch_text.stroke-190"),sQuery(id+"F8.wireOp",EDGE,"E194.sketch_text.stroke-191"),sQuery(id+"F8.wireOp",EDGE,"E194.sketch_text.stroke-192"),sQuery(id+"F8.wireOp",EDGE,"E194.sketch_text.stroke-193"),sQuery(id+"F8.wireOp",EDGE,"E194.sketch_text.stroke-194"),sQuery(id+"F8.wireOp",EDGE,"E194.sketch_text.stroke-195"),sQuery(id+"F8.wireOp",EDGE,"E194.sketch_text.stroke-196"),sQuery(id+"F8.wireOp",EDGE,"E194.sketch_text.stroke-197"),sQuery(id+"F8.wireOp",EDGE,"E194.sketch_text.stroke-198"),sQuery(id+"F8.wireOp",EDGE,"E194.sketch_text.stroke-199"),sQuery(id+"F8.wireOp",EDGE,"E194.sketch_text.stroke-200"),sQuery(id+"F8.wireOp",EDGE,"E194.sketch_text.stroke-201"),sQuery(id+"F8.wireOp",EDGE,"E194.sketch_text.stroke-202"),sQuery(id+"F8.wireOp",EDGE,"E194.sketch_text.stroke-203"),sQuery(id+"F8.wireOp",EDGE,"E194.sketch_text.stroke-204"),sQuery(id+"F8.wireOp",EDGE,"E194.sketch_text.stroke-205"),sQuery(id+"F8.wireOp",EDGE,"E194.sketch_text.stroke-206"),sQuery(id+"F8.wireOp",EDGE,"E194.sketch_text.stroke-207"),sQuery(id+"F8.wireOp",EDGE,"E194.sketch_text.stroke-208"),sQuery(id+"F8.wireOp",EDGE,"E194.sketch_text.stroke-209"),sQuery(id+"F8.wireOp",EDGE,"E194.sketch_text.stroke-210"),sQuery(id+"F8.wireOp",EDGE,"E194.sketch_text.stroke-211"),sQuery(id+"F8.wireOp",EDGE,"E194.sketch_text.stroke-212"),sQuery(id+"F8.wireOp",EDGE,"E194.sketch_text.stroke-213"),sQuery(id+"F8.wireOp",EDGE,"E194.sketch_text.stroke-214"),sQuery(id+"F8.wireOp",EDGE,"E194.sketch_text.stroke-215"),sQuery(id+"F8.wireOp",EDGE,"E194.sketch_text.stroke-216"),sQuery(id+"F8.wireOp",EDGE,"E194.sketch_text.stroke-217"),sQuery(id+"F8.wireOp",EDGE,"E194.sketch_text.stroke-218"),sQuery(id+"F8.wireOp",EDGE,"E194.sketch_text.stroke-219"),sQuery(id+"F8.wireOp",EDGE,"E194.sketch_text.stroke-220"),sQuery(id+"F8.wireOp",EDGE,"E194.sketch_text.stroke-221"),sQuery(id+"F8.wireOp",EDGE,"E194.sketch_text.stroke-222"),sQuery(id+"F8.wireOp",EDGE,"E194.sketch_text.stroke-223")])],"isStart":false});
            var Q14;
            Q14=makeQuery(id+"F9.opExtrude","CAP_FACE",FACE,{"disambiguationData":[OSD([sQuery(id+"F8.wireOp",EDGE,"E194.sketch_text.stroke-167"),sQuery(id+"F8.wireOp",EDGE,"E194.sketch_text.stroke-168"),sQuery(id+"F8.wireOp",EDGE,"E194.sketch_text.stroke-169"),sQuery(id+"F8.wireOp",EDGE,"E194.sketch_text.stroke-170"),sQuery(id+"F8.wireOp",EDGE,"E194.sketch_text.stroke-171"),sQuery(id+"F8.wireOp",EDGE,"E194.sketch_text.stroke-172"),sQuery(id+"F8.wireOp",EDGE,"E194.sketch_text.stroke-173"),sQuery(id+"F8.wireOp",EDGE,"E194.sketch_text.stroke-174"),sQuery(id+"F8.wireOp",EDGE,"E194.sketch_text.stroke-175"),sQuery(id+"F8.wireOp",EDGE,"E194.sketch_text.stroke-176"),sQuery(id+"F8.wireOp",EDGE,"E194.sketch_text.stroke-177"),sQuery(id+"F8.wireOp",EDGE,"E194.sketch_text.stroke-178"),sQuery(id+"F8.wireOp",EDGE,"E194.sketch_text.stroke-179"),sQuery(id+"F8.wireOp",EDGE,"E194.sketch_text.stroke-180"),sQuery(id+"F8.wireOp",EDGE,"E194.sketch_text.stroke-181"),sQuery(id+"F8.wireOp",EDGE,"E194.sketch_text.stroke-182"),sQuery(id+"F8.wireOp",EDGE,"E194.sketch_text.stroke-183"),sQuery(id+"F8.wireOp",EDGE,"E194.sketch_text.stroke-184"),sQuery(id+"F8.wireOp",EDGE,"E194.sketch_text.stroke-185"),sQuery(id+"F8.wireOp",EDGE,"E194.sketch_text.stroke-186"),sQuery(id+"F8.wireOp",EDGE,"E194.sketch_text.stroke-187")])],"isStart":false});
            var Q15;
            Q15=makeQuery(id+"F9.opExtrude","CAP_FACE",FACE,{"disambiguationData":[OSD([sQuery(id+"F8.wireOp",EDGE,"E194.sketch_text.stroke-146"),sQuery(id+"F8.wireOp",EDGE,"E194.sketch_text.stroke-147"),sQuery(id+"F8.wireOp",EDGE,"E194.sketch_text.stroke-148"),sQuery(id+"F8.wireOp",EDGE,"E194.sketch_text.stroke-149"),sQuery(id+"F8.wireOp",EDGE,"E194.sketch_text.stroke-150"),sQuery(id+"F8.wireOp",EDGE,"E194.sketch_text.stroke-151"),sQuery(id+"F8.wireOp",EDGE,"E194.sketch_text.stroke-152"),sQuery(id+"F8.wireOp",EDGE,"E194.sketch_text.stroke-153"),sQuery(id+"F8.wireOp",EDGE,"E194.sketch_text.stroke-154"),sQuery(id+"F8.wireOp",EDGE,"E194.sketch_text.stroke-155"),sQuery(id+"F8.wireOp",EDGE,"E194.sketch_text.stroke-156"),sQuery(id+"F8.wireOp",EDGE,"E194.sketch_text.stroke-157"),sQuery(id+"F8.wireOp",EDGE,"E194.sketch_text.stroke-158"),sQuery(id+"F8.wireOp",EDGE,"E194.sketch_text.stroke-159"),sQuery(id+"F8.wireOp",EDGE,"E194.sketch_text.stroke-160"),sQuery(id+"F8.wireOp",EDGE,"E194.sketch_text.stroke-161"),sQuery(id+"F8.wireOp",EDGE,"E194.sketch_text.stroke-162"),sQuery(id+"F8.wireOp",EDGE,"E194.sketch_text.stroke-163"),sQuery(id+"F8.wireOp",EDGE,"E194.sketch_text.stroke-164"),sQuery(id+"F8.wireOp",EDGE,"E194.sketch_text.stroke-165"),sQuery(id+"F8.wireOp",EDGE,"E194.sketch_text.stroke-166")])],"isStart":false});
            var Q16;
            Q16=makeQuery(id+"F9.opExtrude","CAP_FACE",FACE,{"disambiguationData":[OSD([sQuery(id+"F8.wireOp",EDGE,"E194.sketch_text.stroke-130"),sQuery(id+"F8.wireOp",EDGE,"E194.sketch_text.stroke-131"),sQuery(id+"F8.wireOp",EDGE,"E194.sketch_text.stroke-132"),sQuery(id+"F8.wireOp",EDGE,"E194.sketch_text.stroke-133"),sQuery(id+"F8.wireOp",EDGE,"E194.sketch_text.stroke-134"),sQuery(id+"F8.wireOp",EDGE,"E194.sketch_text.stroke-135"),sQuery(id+"F8.wireOp",EDGE,"E194.sketch_text.stroke-136"),sQuery(id+"F8.wireOp",EDGE,"E194.sketch_text.stroke-137"),sQuery(id+"F8.wireOp",EDGE,"E194.sketch_text.stroke-138"),sQuery(id+"F8.wireOp",EDGE,"E194.sketch_text.stroke-139"),sQuery(id+"F8.wireOp",EDGE,"E194.sketch_text.stroke-140"),sQuery(id+"F8.wireOp",EDGE,"E194.sketch_text.stroke-141"),sQuery(id+"F8.wireOp",EDGE,"E194.sketch_text.stroke-142"),sQuery(id+"F8.wireOp",EDGE,"E194.sketch_text.stroke-143"),sQuery(id+"F8.wireOp",EDGE,"E194.sketch_text.stroke-144"),sQuery(id+"F8.wireOp",EDGE,"E194.sketch_text.stroke-145")])],"isStart":false});
            var Q17;
            Q17=makeQuery(id+"F9.opExtrude","CAP_FACE",FACE,{"disambiguationData":[OSD([sQuery(id+"F8.wireOp",EDGE,"E194.sketch_text.stroke-109"),sQuery(id+"F8.wireOp",EDGE,"E194.sketch_text.stroke-110"),sQuery(id+"F8.wireOp",EDGE,"E194.sketch_text.stroke-111"),sQuery(id+"F8.wireOp",EDGE,"E194.sketch_text.stroke-112"),sQuery(id+"F8.wireOp",EDGE,"E194.sketch_text.stroke-113"),sQuery(id+"F8.wireOp",EDGE,"E194.sketch_text.stroke-114"),sQuery(id+"F8.wireOp",EDGE,"E194.sketch_text.stroke-115"),sQuery(id+"F8.wireOp",EDGE,"E194.sketch_text.stroke-116"),sQuery(id+"F8.wireOp",EDGE,"E194.sketch_text.stroke-117"),sQuery(id+"F8.wireOp",EDGE,"E194.sketch_text.stroke-118"),sQuery(id+"F8.wireOp",EDGE,"E194.sketch_text.stroke-119"),sQuery(id+"F8.wireOp",EDGE,"E194.sketch_text.stroke-120"),sQuery(id+"F8.wireOp",EDGE,"E194.sketch_text.stroke-121"),sQuery(id+"F8.wireOp",EDGE,"E194.sketch_text.stroke-122"),sQuery(id+"F8.wireOp",EDGE,"E194.sketch_text.stroke-123"),sQuery(id+"F8.wireOp",EDGE,"E194.sketch_text.stroke-124"),sQuery(id+"F8.wireOp",EDGE,"E194.sketch_text.stroke-125"),sQuery(id+"F8.wireOp",EDGE,"E194.sketch_text.stroke-126"),sQuery(id+"F8.wireOp",EDGE,"E194.sketch_text.stroke-127"),sQuery(id+"F8.wireOp",EDGE,"E194.sketch_text.stroke-128"),sQuery(id+"F8.wireOp",EDGE,"E194.sketch_text.stroke-129")])],"isStart":false});
            var Q18;
            Q18=makeQuery(id+"F9.opExtrude","CAP_FACE",FACE,{"disambiguationData":[OSD([sQuery(id+"F8.wireOp",EDGE,"E194.sketch_text.stroke-80"),sQuery(id+"F8.wireOp",EDGE,"E194.sketch_text.stroke-81"),sQuery(id+"F8.wireOp",EDGE,"E194.sketch_text.stroke-82"),sQuery(id+"F8.wireOp",EDGE,"E194.sketch_text.stroke-83"),sQuery(id+"F8.wireOp",EDGE,"E194.sketch_text.stroke-84"),sQuery(id+"F8.wireOp",EDGE,"E194.sketch_text.stroke-85"),sQuery(id+"F8.wireOp",EDGE,"E194.sketch_text.stroke-86"),sQuery(id+"F8.wireOp",EDGE,"E194.sketch_text.stroke-87"),sQuery(id+"F8.wireOp",EDGE,"E194.sketch_text.stroke-88"),sQuery(id+"F8.wireOp",EDGE,"E194.sketch_text.stroke-89"),sQuery(id+"F8.wireOp",EDGE,"E194.sketch_text.stroke-90"),sQuery(id+"F8.wireOp",EDGE,"E194.sketch_text.stroke-91"),sQuery(id+"F8.wireOp",EDGE,"E194.sketch_text.stroke-92"),sQuery(id+"F8.wireOp",EDGE,"E194.sketch_text.stroke-93"),sQuery(id+"F8.wireOp",EDGE,"E194.sketch_text.stroke-94"),sQuery(id+"F8.wireOp",EDGE,"E194.sketch_text.stroke-95"),sQuery(id+"F8.wireOp",EDGE,"E194.sketch_text.stroke-96"),sQuery(id+"F8.wireOp",EDGE,"E194.sketch_text.stroke-97"),sQuery(id+"F8.wireOp",EDGE,"E194.sketch_text.stroke-98"),sQuery(id+"F8.wireOp",EDGE,"E194.sketch_text.stroke-99"),sQuery(id+"F8.wireOp",EDGE,"E194.sketch_text.stroke-100"),sQuery(id+"F8.wireOp",EDGE,"E194.sketch_text.stroke-101"),sQuery(id+"F8.wireOp",EDGE,"E194.sketch_text.stroke-102"),sQuery(id+"F8.wireOp",EDGE,"E194.sketch_text.stroke-103"),sQuery(id+"F8.wireOp",EDGE,"E194.sketch_text.stroke-104"),sQuery(id+"F8.wireOp",EDGE,"E194.sketch_text.stroke-105"),sQuery(id+"F8.wireOp",EDGE,"E194.sketch_text.stroke-106"),sQuery(id+"F8.wireOp",EDGE,"E194.sketch_text.stroke-107"),sQuery(id+"F8.wireOp",EDGE,"E194.sketch_text.stroke-108")])],"isStart":false});
            var Q19;
            Q19=makeQuery(id+"F9.opExtrude","CAP_FACE",FACE,{"disambiguationData":[OSD([sQuery(id+"F8.wireOp",EDGE,"E194.sketch_text.stroke-56"),sQuery(id+"F8.wireOp",EDGE,"E194.sketch_text.stroke-57"),sQuery(id+"F8.wireOp",EDGE,"E194.sketch_text.stroke-58"),sQuery(id+"F8.wireOp",EDGE,"E194.sketch_text.stroke-59"),sQuery(id+"F8.wireOp",EDGE,"E194.sketch_text.stroke-60"),sQuery(id+"F8.wireOp",EDGE,"E194.sketch_text.stroke-61"),sQuery(id+"F8.wireOp",EDGE,"E194.sketch_text.stroke-62"),sQuery(id+"F8.wireOp",EDGE,"E194.sketch_text.stroke-63"),sQuery(id+"F8.wireOp",EDGE,"E194.sketch_text.stroke-64"),sQuery(id+"F8.wireOp",EDGE,"E194.sketch_text.stroke-65"),sQuery(id+"F8.wireOp",EDGE,"E194.sketch_text.stroke-66"),sQuery(id+"F8.wireOp",EDGE,"E194.sketch_text.stroke-67"),sQuery(id+"F8.wireOp",EDGE,"E194.sketch_text.stroke-68"),sQuery(id+"F8.wireOp",EDGE,"E194.sketch_text.stroke-69"),sQuery(id+"F8.wireOp",EDGE,"E194.sketch_text.stroke-70"),sQuery(id+"F8.wireOp",EDGE,"E194.sketch_text.stroke-71"),sQuery(id+"F8.wireOp",EDGE,"E194.sketch_text.stroke-72"),sQuery(id+"F8.wireOp",EDGE,"E194.sketch_text.stroke-73"),sQuery(id+"F8.wireOp",EDGE,"E194.sketch_text.stroke-74"),sQuery(id+"F8.wireOp",EDGE,"E194.sketch_text.stroke-75"),sQuery(id+"F8.wireOp",EDGE,"E194.sketch_text.stroke-76"),sQuery(id+"F8.wireOp",EDGE,"E194.sketch_text.stroke-77"),sQuery(id+"F8.wireOp",EDGE,"E194.sketch_text.stroke-78"),sQuery(id+"F8.wireOp",EDGE,"E194.sketch_text.stroke-79")])],"isStart":false});
            var Q20;
            Q20=makeQuery(id+"F9.opExtrude","CAP_FACE",FACE,{"disambiguationData":[OSD([sQuery(id+"F8.wireOp",EDGE,"E194.sketch_text.stroke-36"),sQuery(id+"F8.wireOp",EDGE,"E194.sketch_text.stroke-37"),sQuery(id+"F8.wireOp",EDGE,"E194.sketch_text.stroke-38"),sQuery(id+"F8.wireOp",EDGE,"E194.sketch_text.stroke-39"),sQuery(id+"F8.wireOp",EDGE,"E194.sketch_text.stroke-40"),sQuery(id+"F8.wireOp",EDGE,"E194.sketch_text.stroke-41"),sQuery(id+"F8.wireOp",EDGE,"E194.sketch_text.stroke-42"),sQuery(id+"F8.wireOp",EDGE,"E194.sketch_text.stroke-43"),sQuery(id+"F8.wireOp",EDGE,"E194.sketch_text.stroke-44"),sQuery(id+"F8.wireOp",EDGE,"E194.sketch_text.stroke-45"),sQuery(id+"F8.wireOp",EDGE,"E194.sketch_text.stroke-46"),sQuery(id+"F8.wireOp",EDGE,"E194.sketch_text.stroke-47"),sQuery(id+"F8.wireOp",EDGE,"E194.sketch_text.stroke-48"),sQuery(id+"F8.wireOp",EDGE,"E194.sketch_text.stroke-49"),sQuery(id+"F8.wireOp",EDGE,"E194.sketch_text.stroke-50"),sQuery(id+"F8.wireOp",EDGE,"E194.sketch_text.stroke-51"),sQuery(id+"F8.wireOp",EDGE,"E194.sketch_text.stroke-52"),sQuery(id+"F8.wireOp",EDGE,"E194.sketch_text.stroke-53"),sQuery(id+"F8.wireOp",EDGE,"E194.sketch_text.stroke-54"),sQuery(id+"F8.wireOp",EDGE,"E194.sketch_text.stroke-55")])],"isStart":false});
            var Q21;
            Q21=makeQuery(id+"F9.opExtrude","CAP_FACE",FACE,{"disambiguationData":[OSD([sQuery(id+"F8.wireOp",EDGE,"E194.sketch_text.stroke-0"),sQuery(id+"F8.wireOp",EDGE,"E194.sketch_text.stroke-1"),sQuery(id+"F8.wireOp",EDGE,"E194.sketch_text.stroke-2"),sQuery(id+"F8.wireOp",EDGE,"E194.sketch_text.stroke-3"),sQuery(id+"F8.wireOp",EDGE,"E194.sketch_text.stroke-4"),sQuery(id+"F8.wireOp",EDGE,"E194.sketch_text.stroke-5"),sQuery(id+"F8.wireOp",EDGE,"E194.sketch_text.stroke-6"),sQuery(id+"F8.wireOp",EDGE,"E194.sketch_text.stroke-7"),sQuery(id+"F8.wireOp",EDGE,"E194.sketch_text.stroke-8"),sQuery(id+"F8.wireOp",EDGE,"E194.sketch_text.stroke-9"),sQuery(id+"F8.wireOp",EDGE,"E194.sketch_text.stroke-10"),sQuery(id+"F8.wireOp",EDGE,"E194.sketch_text.stroke-11"),sQuery(id+"F8.wireOp",EDGE,"E194.sketch_text.stroke-12"),sQuery(id+"F8.wireOp",EDGE,"E194.sketch_text.stroke-13"),sQuery(id+"F8.wireOp",EDGE,"E194.sketch_text.stroke-14"),sQuery(id+"F8.wireOp",EDGE,"E194.sketch_text.stroke-15"),sQuery(id+"F8.wireOp",EDGE,"E194.sketch_text.stroke-16"),sQuery(id+"F8.wireOp",EDGE,"E194.sketch_text.stroke-17"),sQuery(id+"F8.wireOp",EDGE,"E194.sketch_text.stroke-18"),sQuery(id+"F8.wireOp",EDGE,"E194.sketch_text.stroke-19"),sQuery(id+"F8.wireOp",EDGE,"E194.sketch_text.stroke-20"),sQuery(id+"F8.wireOp",EDGE,"E194.sketch_text.stroke-21"),sQuery(id+"F8.wireOp",EDGE,"E194.sketch_text.stroke-22"),sQuery(id+"F8.wireOp",EDGE,"E194.sketch_text.stroke-23"),sQuery(id+"F8.wireOp",EDGE,"E194.sketch_text.stroke-24"),sQuery(id+"F8.wireOp",EDGE,"E194.sketch_text.stroke-25"),sQuery(id+"F8.wireOp",EDGE,"E194.sketch_text.stroke-26"),sQuery(id+"F8.wireOp",EDGE,"E194.sketch_text.stroke-27"),sQuery(id+"F8.wireOp",EDGE,"E194.sketch_text.stroke-28"),sQuery(id+"F8.wireOp",EDGE,"E194.sketch_text.stroke-29"),sQuery(id+"F8.wireOp",EDGE,"E194.sketch_text.stroke-30"),sQuery(id+"F8.wireOp",EDGE,"E194.sketch_text.stroke-31"),sQuery(id+"F8.wireOp",EDGE,"E194.sketch_text.stroke-32"),sQuery(id+"F8.wireOp",EDGE,"E194.sketch_text.stroke-33"),sQuery(id+"F8.wireOp",EDGE,"E194.sketch_text.stroke-34"),sQuery(id+"F8.wireOp",EDGE,"E194.sketch_text.stroke-35")])],"isStart":false});
            extrude(context, id + "F19", {"entities" : qUnion([Q0, Q1, Q2, Q3, Q4, Q5, Q6, Q7, Q8, Q9, Q10, Q11, Q12, Q13, Q14, Q15, Q16, Q17, Q18, Q19, Q20, Q21]), "operationType" : NewBodyOperationType.ADD, "depth" : 1 * mm});
        }
        {
            var Q0;
            Q0=makeQuery(id+"F4.opExtrude","CAP_FACE",FACE,{"disambiguationData":[OSD([sQuery(id+"F2.wireOp",EDGE,"E4")])],"isStart":false});
            extrude(context, id + "F20", {"entities" : qUnion([Q0]), "operationType" : NewBodyOperationType.ADD, "depth" : 1 * mm});
        }
        {
            var Q0;
            {var subQ0=sQuery(id+"F0.wireOp",EDGE,"E3");var subQ1=sQuery(id+"F0.wireOp",EDGE,"E2");var subQ2=sQuery(id+"F0.wireOp",EDGE,"E1");var subQ3=sQuery(id+"F0.wireOp",EDGE,"E0");Q0=makeQuery(id+"F6.boolean.opBoolean","MERGE",FACE,{"derivedFrom":[makeQuery(id+"F1.opExtrude","CAP_FACE",FACE,{"disambiguationData":[OSD([subQ3,subQ2,subQ1,subQ0])],"isStart":true}),makeQuery(id+"F6.opExtrude","CAP_FACE",FACE,{"disambiguationData":[OSD([subQ3,subQ2,subQ1,subQ0])],"isStart":false})]});}
            extrude(context, id + "F21", {"entities" : qUnion([Q0]), "operationType" : NewBodyOperationType.ADD, "depth" : 4 * mm});
        }
        {
            var Q0;
            {var subQ189=sQuery(id+"F5.wireOp",EDGE,"E190");var subQ190=sQuery(id+"F5.wireOp",EDGE,"E179.0");var subQ191=sQuery(id+"F0.wireOp",EDGE,"E2");var subQ256=sQuery(id+"F5.wireOp",EDGE,"E183");var subQ284=sQuery(id+"F0.wireOp",EDGE,"E1");var subQ290=sQuery(id+"F5.wireOp",EDGE,"E188");var subQ297=sQuery(id+"F5.wireOp",EDGE,"E182");var subQ303=sQuery(id+"F0.wireOp",EDGE,"E3");var subQ316=sQuery(id+"F0.wireOp",EDGE,"E0");var subQ317=makeQuery(id+"F1.opExtrude","SWEPT_FACE",FACE,{"disambiguationData":[OSD([subQ316])]});var subQ322=sQuery(id+"F5.wireOp",EDGE,"E187");var subQ334=sQuery(id+"F5.wireOp",EDGE,"E189");var subQ342=sQuery(id+"F5.wireOp",EDGE,"E186");var subQ343=sQuery(id+"F5.wireOp",EDGE,"E184");var subQ363=sQuery(id+"F5.wireOp",EDGE,"E180");var subQ367=sQuery(id+"F5.wireOp",EDGE,"E181");var subQ467=sQuery(id+"F5.wireOp",EDGE,"E178.0");Q0=makeQuery(id+"F13.boolean.opBoolean","SPLIT",FACE,{"disambiguationData":[TD([subQ317])],"derivedFrom":makeQuery(id+"F9.boolean.opBoolean","SPLIT",FACE,{"disambiguationData":[TD([subQ317])],"derivedFrom":makeQuery(id+"F6.boolean.opBoolean","MERGE",FACE,{"derivedFrom":[makeQuery(id+"F3.boolean.opBoolean","SPLIT",FACE,{"disambiguationData":[TD([subQ317])],"derivedFrom":makeQuery(id+"F1.opExtrude","CAP_FACE",FACE,{"disambiguationData":[OSD([subQ316,subQ284,subQ191,subQ303])],"isStart":false})}),makeQuery(id+"F6.opExtrude","CAP_FACE",FACE,{"disambiguationData":[OSD([subQ467,subQ190,subQ363,subQ367,subQ297,subQ256,subQ343,subQ342,subQ322,subQ290,subQ334,subQ189])],"isStart":true})]})})});}
            var sketch = newSketch(context, id + "F22", { "sketchPlane" : qUnion([Q0])});
            skLineSegment(sketch, "E206", {"start": v(0.82, -96.98) * mm, "end": v(0.82, -71.63) * mm, "construction": true});
            skCircle(sketch, "E207.cCircle", {"center": v(38.32, -84.98) * mm, "radius": 2.85 * mm, "construction": true});
            skLineSegment(sketch, "E207.0", {"start": v(36.67, -82.13) * mm, "end": v(39.97, -82.13) * mm});
            skLineSegment(sketch, "E207.1", {"start": v(39.97, -82.13) * mm, "end": v(41.61, -84.98) * mm});
            skLineSegment(sketch, "E207.2", {"start": v(41.61, -84.98) * mm, "end": v(39.97, -87.83) * mm, "construction": true});
            skLineSegment(sketch, "E207.3", {"start": v(39.97, -87.83) * mm, "end": v(36.67, -87.83) * mm, "construction": true});
            skLineSegment(sketch, "E207.4", {"start": v(36.67, -87.83) * mm, "end": v(35.03, -84.98) * mm, "construction": true});
            skLineSegment(sketch, "E207.5", {"start": v(35.03, -84.98) * mm, "end": v(36.67, -82.13) * mm});
            skPoint(sketch, "E207.0.midPoint", {"position": v(38.32, -82.13) * mm});
            skLineSegment(sketch, "E208.1.0.0", {"start": v(-0.83, -82.13) * mm, "end": v(2.47, -82.13) * mm});
            skPoint(sketch, "E208.1.0.1", {"position": v(0.82, -82.13) * mm});
            skCircle(sketch, "E208.1.0.2", {"center": v(0.82, -84.98) * mm, "radius": 2.85 * mm, "construction": true});
            skLineSegment(sketch, "E208.1.0.3", {"start": v(2.47, -87.83) * mm, "end": v(-0.83, -87.83) * mm, "construction": true});
            skLineSegment(sketch, "E208.1.0.4", {"start": v(-0.83, -87.83) * mm, "end": v(-2.47, -84.98) * mm, "construction": true});
            skLineSegment(sketch, "E208.1.0.5", {"start": v(4.11, -84.98) * mm, "end": v(2.47, -87.83) * mm, "construction": true});
            skLineSegment(sketch, "E208.1.0.6", {"start": v(2.47, -82.13) * mm, "end": v(4.11, -84.98) * mm});
            skLineSegment(sketch, "E208.1.0.7", {"start": v(-2.47, -84.98) * mm, "end": v(-0.83, -82.13) * mm});
            skLineSegment(sketch, "E208.2.0.0", {"start": v(-38.33, -82.13) * mm, "end": v(-35.03, -82.13) * mm});
            skPoint(sketch, "E208.2.0.1", {"position": v(-36.68, -82.13) * mm});
            skCircle(sketch, "E208.2.0.2", {"center": v(-36.68, -84.98) * mm, "radius": 2.85 * mm, "construction": true});
            skLineSegment(sketch, "E208.2.0.3", {"start": v(-35.03, -87.83) * mm, "end": v(-38.33, -87.83) * mm, "construction": true});
            skLineSegment(sketch, "E208.2.0.4", {"start": v(-38.33, -87.83) * mm, "end": v(-39.97, -84.98) * mm, "construction": true});
            skLineSegment(sketch, "E208.2.0.5", {"start": v(-33.39, -84.98) * mm, "end": v(-35.03, -87.83) * mm, "construction": true});
            skLineSegment(sketch, "E208.2.0.6", {"start": v(-35.03, -82.13) * mm, "end": v(-33.39, -84.98) * mm});
            skLineSegment(sketch, "E208.2.0.7", {"start": v(-39.97, -84.98) * mm, "end": v(-38.33, -82.13) * mm});
            skLineSegment(sketch, "E208.direction1", {"start": v(36.67, -87.83) * mm, "end": v(-0.83, -87.83) * mm, "construction": true});
            skLineSegment(sketch, "E209", {"start": v(41.61, -84.98) * mm, "end": v(41.61, -96.98) * mm});
            skLineSegment(sketch, "E210.0", {"start": v(41.61, -96.98) * mm, "end": v(35.03, -96.98) * mm});
            skLineSegment(sketch, "E211", {"start": v(35.03, -84.98) * mm, "end": v(35.03, -96.98) * mm});
            skLineSegment(sketch, "E212", {"start": v(4.11, -84.98) * mm, "end": v(4.11, -96.98) * mm});
            skLineSegment(sketch, "E213", {"start": v(-2.47, -84.98) * mm, "end": v(-2.47, -96.98) * mm});
            skLineSegment(sketch, "E214", {"start": v(-33.39, -84.98) * mm, "end": v(-33.39, -96.98) * mm});
            skLineSegment(sketch, "E215", {"start": v(-39.97, -84.98) * mm, "end": v(-39.9, -96.98) * mm});
            skPoint(sketch, "E216.orphan", {"position": v(-44.18, -96.98) * mm});
            skLineSegment(sketch, "E217.trimOffspring", {"start": v(-33.39, -96.98) * mm, "end": v(-39.9, -96.98) * mm});
            skPoint(sketch, "E218.orphan", {"position": v(45.82, -96.98) * mm});
            skLineSegment(sketch, "E219.trimOffspring", {"start": v(4.11, -96.98) * mm, "end": v(-2.47, -96.98) * mm});
            skSolve(sketch);
        }
        {
            var Q0;
            Q0 = qSketchRegion(id + "F22", true);
            extrude(context, id + "F23", {"entities" : qUnion([Q0]), "operationType" : NewBodyOperationType.REMOVE, "oppositeDirection" : true, "depth" : 4 * mm, "hasSecondDirection" : true, "secondDirectionOppositeDirection" : true, "secondDirectionDepth" : 1 * mm});
        }
        {
            var Q0;
            Q0=makeQuery(id+"F23.boolean.opBoolean","COPY",FACE,{"derivedFrom":makeQuery(id+"F23.opExtrude","CAP_FACE",FACE,{"disambiguationData":[OSD([sQuery(id+"F22.wireOp",EDGE,"E208.1.0.0"),sQuery(id+"F22.wireOp",EDGE,"E208.1.0.6"),sQuery(id+"F22.wireOp",EDGE,"E208.1.0.7"),sQuery(id+"F22.wireOp",EDGE,"E212"),sQuery(id+"F22.wireOp",EDGE,"E213"),sQuery(id+"F22.wireOp",EDGE,"E219.trimOffspring")])],"isStart":false})});
            var sketch = newSketch(context, id + "F24", { "sketchPlane" : qUnion([Q0])});
            skCircle(sketch, "E220.0", {"center": v(-36.68, -84.98) * mm, "radius": 2.85 * mm, "construction": true});
            skCircle(sketch, "E221", {"center": v(-36.68, -84.98) * mm, "radius": 1.75 * mm});
            skCircle(sketch, "E222.1.0.0", {"center": v(0.82, -84.98) * mm, "radius": 1.75 * mm});
            skCircle(sketch, "E222.2.0.0", {"center": v(38.32, -84.98) * mm, "radius": 1.75 * mm});
            skLineSegment(sketch, "E222.direction1", {"start": v(-36.68, -84.98) * mm, "end": v(0.82, -84.98) * mm, "construction": true});
            skSolve(sketch);
        }
        {
            var Q0;
            Q0 = qSketchRegion(id + "F24", true);
            extrude(context, id + "F25", {"entities" : qUnion([Q0]), "operationType" : NewBodyOperationType.REMOVE, "oppositeDirection" : true, "depth" : 25 * mm});
        }
    });
